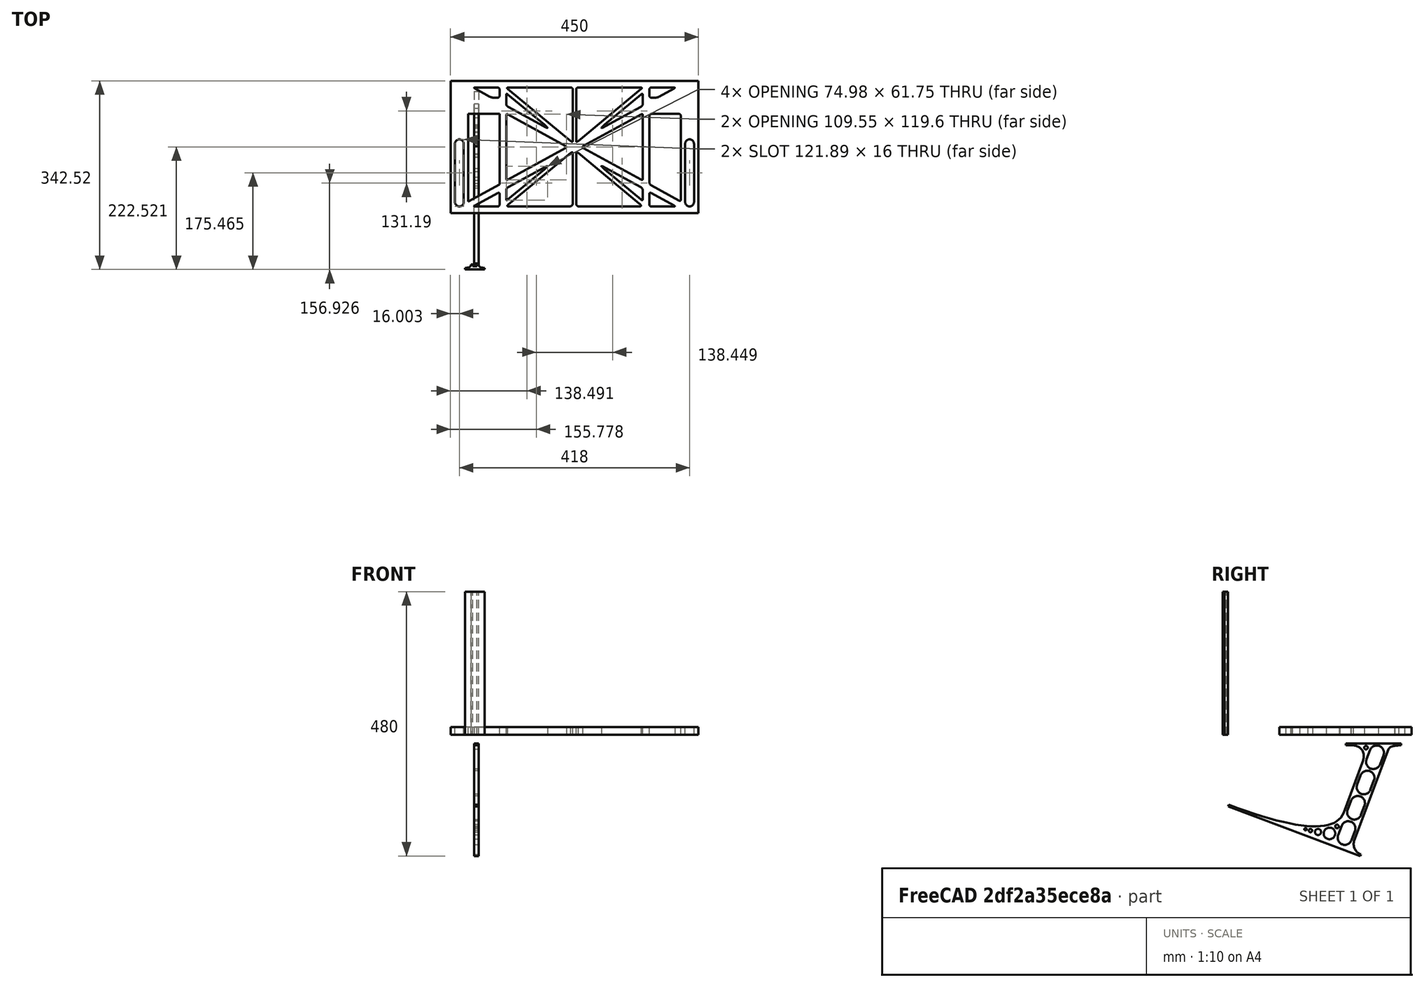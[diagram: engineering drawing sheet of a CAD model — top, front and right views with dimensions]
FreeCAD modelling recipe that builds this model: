
FCSTD DOCUMENT  (FreeCAD 0.19R0.19.2)
Label: laptopStand149FCStd
License: All rights reserved
LicenseURL: http://en.wikipedia.org/wiki/All_rights_reserved
objects: Sketcher::SketchObject×4, Part::Extrusion×3
note: 7 computed .brp shape members not serialized (recipe doc carries the construction recipe); baked Part::Feature solids carry a one-line shape summary decoded from their .brp

FEATURE [Sketcher::SketchObject] Sketch
  FullyConstrained = false
  sketch-geometry (349):
    g0: LineSegment StartX=-10.9272 StartY=-82.7794 StartZ=0 EndX=46.0728 EndY=-51.4823 EndZ=0
    g1: LineSegment StartX=-10.9272 StartY=76.4095 StartZ=0 EndX=-10.9272 EndY=-82.7794 EndZ=0
    g2: LineSegment StartX=46.0728 StartY=76.4095 StartZ=0 EndX=46.0728 EndY=-51.4823 EndZ=0
    g3: LineSegment StartX=-42.9272 StartY=136.221 StartZ=0 EndX=-42.9272 EndY=-103.779 EndZ=0
    g4: LineSegment StartX=407.073 StartY=136.221 StartZ=0 EndX=407.073 EndY=-103.779 EndZ=0
    g5: ArcOfCircle CenterX=-26.9272 CenterY=-83.7794 CenterZ=0 NormalX=0 NormalY=0 NormalZ=1 AngleXU=0 Radius=8 StartAngle=3.14159 EndAngle=6.28319
    g6: ArcOfCircle CenterX=391.073 CenterY=22.1087 CenterZ=0 NormalX=0 NormalY=0 NormalZ=1 AngleXU=0 Radius=8 StartAngle=-4.4e-15 EndAngle=3.14159
    g7: LineSegment StartX=399.073 StartY=22.1087 StartZ=0 EndX=399.073 EndY=-83.7794 EndZ=0
    g8: LineSegment StartX=383.073 StartY=22.1087 StartZ=0 EndX=383.073 EndY=-83.7794 EndZ=0
    g9: ArcOfCircle CenterX=391.073 CenterY=-83.7794 CenterZ=0 NormalX=0 NormalY=0 NormalZ=1 AngleXU=0 Radius=8 StartAngle=3.14159 EndAngle=6.28319
    g10: Circle CenterX=175.022 CenterY=27.0628 CenterZ=0 NormalX=0 NormalY=0 NormalZ=1 AngleXU=0 Radius=1
    g11: Circle CenterX=179.022 CenterY=24.8665 CenterZ=0 NormalX=0 NormalY=0 NormalZ=1 AngleXU=0 Radius=1
    g12: Circle CenterX=179.022 CenterY=27.0628 CenterZ=0 NormalX=0 NormalY=0 NormalZ=1 AngleXU=0 Radius=1
    g13: BSplineCurve PolesCount=3 KnotsCount=2 Degree=2 IsPeriodic=0
    g14: GeomPoint X=175.022 Y=27.0628 Z=0
    g15: GeomPoint X=179.022 Y=27.0628 Z=0
    g16: Circle CenterX=189.124 CenterY=27.0628 CenterZ=0 NormalX=0 NormalY=0 NormalZ=1 AngleXU=0 Radius=1
    g17: Circle CenterX=185.124 CenterY=24.8665 CenterZ=0 NormalX=0 NormalY=0 NormalZ=1 AngleXU=0 Radius=1
    g18: Circle CenterX=185.124 CenterY=27.0628 CenterZ=0 NormalX=0 NormalY=0 NormalZ=1 AngleXU=0 Radius=1
    g19: BSplineCurve PolesCount=3 KnotsCount=2 Degree=2 IsPeriodic=0
    g20: GeomPoint X=189.124 Y=27.0628 Z=0
    g21: GeomPoint X=185.124 Y=27.0628 Z=0
    g22: Circle CenterX=175.022 CenterY=5.37834 CenterZ=0 NormalX=0 NormalY=0 NormalZ=1 AngleXU=0 Radius=1
    g23: Circle CenterX=179.022 CenterY=7.57463 CenterZ=0 NormalX=0 NormalY=0 NormalZ=1 AngleXU=0 Radius=1
    g24: Circle CenterX=179.022 CenterY=5.34704 CenterZ=0 NormalX=0 NormalY=0 NormalZ=1 AngleXU=0 Radius=1
    g25: BSplineCurve PolesCount=3 KnotsCount=2 Degree=2 IsPeriodic=0
    g26: GeomPoint X=175.022 Y=5.37834 Z=0
    g27: GeomPoint X=179.022 Y=5.34704 Z=0
    g28: Circle CenterX=189.124 CenterY=5.37834 CenterZ=0 NormalX=0 NormalY=0 NormalZ=1 AngleXU=0 Radius=1
    g29: Circle CenterX=185.124 CenterY=7.57463 CenterZ=0 NormalX=0 NormalY=0 NormalZ=1 AngleXU=0 Radius=1
    g30: Circle CenterX=185.124 CenterY=5.34704 CenterZ=0 NormalX=0 NormalY=0 NormalZ=1 AngleXU=0 Radius=1
    g31: BSplineCurve PolesCount=3 KnotsCount=2 Degree=2 IsPeriodic=0
    g32: GeomPoint X=189.124 Y=5.37834 Z=0
    g33: GeomPoint X=185.124 Y=5.34704 Z=0
    g34: Circle CenterX=165.871 CenterY=18.1458 CenterZ=0 NormalX=0 NormalY=0 NormalZ=1 AngleXU=0 Radius=1
    g35: Circle CenterX=169.377 CenterY=16.2206 CenterZ=0 NormalX=0 NormalY=0 NormalZ=1 AngleXU=0 Radius=1
    g36: Circle CenterX=165.871 CenterY=14.2954 CenterZ=0 NormalX=0 NormalY=0 NormalZ=1 AngleXU=0 Radius=1
    g37: BSplineCurve PolesCount=3 KnotsCount=2 Degree=2 IsPeriodic=0
    g38: GeomPoint X=165.871 Y=18.1458 Z=0
    g39: GeomPoint X=165.871 Y=14.2954 Z=0
    g40: Circle CenterX=198.275 CenterY=18.1458 CenterZ=0 NormalX=0 NormalY=0 NormalZ=1 AngleXU=0 Radius=1
    g41: Circle CenterX=194.768 CenterY=16.2206 CenterZ=0 NormalX=0 NormalY=0 NormalZ=1 AngleXU=0 Radius=1
    g42: Circle CenterX=198.275 CenterY=14.2954 CenterZ=0 NormalX=0 NormalY=0 NormalZ=1 AngleXU=0 Radius=1
    g43: BSplineCurve PolesCount=3 KnotsCount=2 Degree=2 IsPeriodic=0
    g44: GeomPoint X=198.275 Y=18.1458 Z=0
    g45: GeomPoint X=198.275 Y=14.2954 Z=0
    g46: LineSegment StartX=407.073 StartY=-103.779 StartZ=0 EndX=-42.9272 EndY=-103.779 EndZ=0
    g47: LineSegment StartX=407.073 StartY=136.221 StartZ=0 EndX=-42.9272 EndY=136.221 EndZ=0
    g48: LineSegment StartX=46.0728 StartY=76.4095 StartZ=0 EndX=-10.9272 EndY=76.4095 EndZ=0
    g49: Circle CenterX=125.607 CenterY=54.1951 CenterZ=0 NormalX=0 NormalY=0 NormalZ=1 AngleXU=0 Radius=1
    g50: Circle CenterX=139.632 CenterY=46.4944 CenterZ=0 NormalX=0 NormalY=0 NormalZ=1 AngleXU=0 Radius=1
    g51: Circle CenterX=127.326 CenterY=56.7187 CenterZ=0 NormalX=0 NormalY=0 NormalZ=1 AngleXU=0 Radius=1
    g52: BSplineCurve PolesCount=3 KnotsCount=2 Degree=2 IsPeriodic=0
    g53: GeomPoint X=125.607 Y=54.1951 Z=0
    g54: GeomPoint X=127.326 Y=56.7187 Z=0
    g55: Circle CenterX=236.821 CenterY=56.7187 CenterZ=0 NormalX=0 NormalY=0 NormalZ=1 AngleXU=0 Radius=1
    g56: Circle CenterX=224.513 CenterY=46.4944 CenterZ=0 NormalX=0 NormalY=0 NormalZ=1 AngleXU=0 Radius=1
    g57: Circle CenterX=238.538 CenterY=54.1951 CenterZ=0 NormalX=0 NormalY=0 NormalZ=1 AngleXU=0 Radius=1
    g58: BSplineCurve PolesCount=3 KnotsCount=2 Degree=2 IsPeriodic=0
    g59: GeomPoint X=236.821 Y=56.7187 Z=0
    g60: GeomPoint X=238.538 Y=54.1951 Z=0
    g61: Circle CenterX=238.538 CenterY=-21.7539 CenterZ=0 NormalX=0 NormalY=0 NormalZ=1 AngleXU=0 Radius=1
    g62: Circle CenterX=224.513 CenterY=-14.0532 CenterZ=0 NormalX=0 NormalY=0 NormalZ=1 AngleXU=0 Radius=1
    g63: Circle CenterX=236.821 CenterY=-24.2775 CenterZ=0 NormalX=0 NormalY=0 NormalZ=1 AngleXU=0 Radius=1
    g64: BSplineCurve PolesCount=3 KnotsCount=2 Degree=2 IsPeriodic=0
    g65: GeomPoint X=238.538 Y=-21.7539 Z=0
    g66: GeomPoint X=236.821 Y=-24.2775 Z=0
    g67: Circle CenterX=125.607 CenterY=-21.7539 CenterZ=0 NormalX=0 NormalY=0 NormalZ=1 AngleXU=0 Radius=1
    g68: Circle CenterX=139.632 CenterY=-14.0532 CenterZ=0 NormalX=0 NormalY=0 NormalZ=1 AngleXU=0 Radius=1
    g69: Circle CenterX=127.325 CenterY=-24.2775 CenterZ=0 NormalX=0 NormalY=0 NormalZ=1 AngleXU=0 Radius=1
    g70: BSplineCurve PolesCount=3 KnotsCount=2 Degree=2 IsPeriodic=0
    g71: GeomPoint X=125.607 Y=-21.7539 Z=0
    g72: GeomPoint X=127.325 Y=-24.2775 Z=0
    g73: Circle CenterX=302.996 CenterY=111.695 CenterZ=0 NormalX=0 NormalY=0 NormalZ=1 AngleXU=0 Radius=1
    g74: Circle CenterX=306.073 CenterY=114.251 CenterZ=0 NormalX=0 NormalY=0 NormalZ=1 AngleXU=0 Radius=1
    g75: Circle CenterX=306.073 CenterY=110.251 CenterZ=0 NormalX=0 NormalY=0 NormalZ=1 AngleXU=0 Radius=1
    g76: BSplineCurve PolesCount=3 KnotsCount=2 Degree=2 IsPeriodic=0
    g77: GeomPoint X=302.996 Y=111.695 Z=0
    g78: GeomPoint X=306.073 Y=110.251 Z=0
    g79: Circle CenterX=306.073 CenterY=95.2763 CenterZ=0 NormalX=0 NormalY=0 NormalZ=1 AngleXU=0 Radius=1
    g80: Circle CenterX=306.073 CenterY=91.2763 CenterZ=0 NormalX=0 NormalY=0 NormalZ=1 AngleXU=0 Radius=1
    g81: Circle CenterX=302.567 CenterY=89.3511 CenterZ=0 NormalX=0 NormalY=0 NormalZ=1 AngleXU=0 Radius=1
    g82: BSplineCurve PolesCount=3 KnotsCount=2 Degree=2 IsPeriodic=0
    g83: GeomPoint X=306.073 Y=95.2763 Z=0
    g84: GeomPoint X=302.567 Y=89.3511 Z=0
    g85: LineSegment StartX=306.073 StartY=110.251 StartZ=0 EndX=306.073 EndY=95.2763 EndZ=0
    g86: LineSegment StartX=302.996 StartY=111.695 StartZ=0 EndX=236.821 EndY=56.7187 EndZ=0
    g87: LineSegment StartX=238.538 StartY=54.1951 StartZ=0 EndX=302.567 EndY=89.3511 EndZ=0
    g88: Circle CenterX=61.1496 CenterY=111.695 CenterZ=0 NormalX=0 NormalY=0 NormalZ=1 AngleXU=0 Radius=1
    g89: Circle CenterX=58.0728 CenterY=114.251 CenterZ=0 NormalX=0 NormalY=0 NormalZ=1 AngleXU=0 Radius=1
    g90: Circle CenterX=58.0728 CenterY=110.251 CenterZ=0 NormalX=0 NormalY=0 NormalZ=1 AngleXU=0 Radius=1
    g91: BSplineCurve PolesCount=3 KnotsCount=2 Degree=2 IsPeriodic=0
    g92: GeomPoint X=61.1496 Y=111.695 Z=0
    g93: GeomPoint X=58.0728 Y=110.251 Z=0
    g94: Circle CenterX=61.5791 CenterY=89.3511 CenterZ=0 NormalX=0 NormalY=0 NormalZ=1 AngleXU=0 Radius=1
    g95: Circle CenterX=58.0728 CenterY=91.2763 CenterZ=0 NormalX=0 NormalY=0 NormalZ=1 AngleXU=0 Radius=1
    g96: Circle CenterX=58.0728 CenterY=95.2763 CenterZ=0 NormalX=0 NormalY=0 NormalZ=1 AngleXU=0 Radius=1
    g97: BSplineCurve PolesCount=3 KnotsCount=2 Degree=2 IsPeriodic=0
    g98: GeomPoint X=61.5791 Y=89.3511 Z=0
    g99: GeomPoint X=58.0728 Y=95.2763 Z=0
    g100: LineSegment StartX=58.0728 StartY=110.251 StartZ=0 EndX=58.0728 EndY=95.2763 EndZ=0
    g101: LineSegment StartX=61.1496 StartY=111.695 StartZ=0 EndX=127.326 EndY=56.7187 EndZ=0
    g102: LineSegment StartX=125.607 StartY=54.1951 StartZ=0 EndX=61.5791 EndY=89.3511 EndZ=0
    g103: Circle CenterX=61.5791 CenterY=-56.9099 CenterZ=0 NormalX=0 NormalY=0 NormalZ=1 AngleXU=0 Radius=1
    g104: Circle CenterX=58.0728 CenterY=-58.8351 CenterZ=0 NormalX=0 NormalY=0 NormalZ=1 AngleXU=0 Radius=1
    g105: Circle CenterX=58.0728 CenterY=-62.8351 CenterZ=0 NormalX=0 NormalY=0 NormalZ=1 AngleXU=0 Radius=1
    g106: BSplineCurve PolesCount=3 KnotsCount=2 Degree=2 IsPeriodic=0
    g107: GeomPoint X=61.5791 Y=-56.9099 Z=0
    g108: GeomPoint X=58.0728 Y=-62.8351 Z=0
    g109: Circle CenterX=58.0728 CenterY=-77.8102 CenterZ=0 NormalX=0 NormalY=0 NormalZ=1 AngleXU=0 Radius=1
    g110: Circle CenterX=58.0728 CenterY=-81.8102 CenterZ=0 NormalX=0 NormalY=0 NormalZ=1 AngleXU=0 Radius=1
    g111: Circle CenterX=61.1496 CenterY=-79.2541 CenterZ=0 NormalX=0 NormalY=0 NormalZ=1 AngleXU=0 Radius=1
    g112: BSplineCurve PolesCount=3 KnotsCount=2 Degree=2 IsPeriodic=0
    g113: GeomPoint X=58.0728 Y=-77.8102 Z=0
    g114: GeomPoint X=61.1496 Y=-79.2541 Z=0
    g115: LineSegment StartX=58.0728 StartY=-62.8351 StartZ=0 EndX=58.0728 EndY=-77.8102 EndZ=0
    g116: LineSegment StartX=61.1496 StartY=-79.2541 StartZ=0 EndX=127.325 EndY=-24.2775 EndZ=0
    g117: LineSegment StartX=125.607 StartY=-21.7539 StartZ=0 EndX=61.5791 EndY=-56.9099 EndZ=0
    g118: Circle CenterX=302.567 CenterY=-56.9099 CenterZ=0 NormalX=0 NormalY=0 NormalZ=1 AngleXU=0 Radius=1
    g119: Circle CenterX=306.073 CenterY=-58.8351 CenterZ=0 NormalX=0 NormalY=0 NormalZ=1 AngleXU=0 Radius=1
    g120: Circle CenterX=306.073 CenterY=-62.8351 CenterZ=0 NormalX=0 NormalY=0 NormalZ=1 AngleXU=0 Radius=1
    g121: BSplineCurve PolesCount=3 KnotsCount=2 Degree=2 IsPeriodic=0
    g122: GeomPoint X=302.567 Y=-56.9099 Z=0
    g123: GeomPoint X=306.073 Y=-62.8351 Z=0
    g124: Circle CenterX=302.996 CenterY=-79.2541 CenterZ=0 NormalX=0 NormalY=0 NormalZ=1 AngleXU=0 Radius=1
    g125: Circle CenterX=306.073 CenterY=-81.8102 CenterZ=0 NormalX=0 NormalY=0 NormalZ=1 AngleXU=0 Radius=1
    g126: Circle CenterX=306.073 CenterY=-77.8102 CenterZ=0 NormalX=0 NormalY=0 NormalZ=1 AngleXU=0 Radius=1
    g127: BSplineCurve PolesCount=3 KnotsCount=2 Degree=2 IsPeriodic=0
    g128: GeomPoint X=302.996 Y=-79.2541 Z=0
    g129: GeomPoint X=306.073 Y=-77.8102 Z=0
    g130: LineSegment StartX=306.073 StartY=-62.8351 StartZ=0 EndX=306.073 EndY=-77.8102 EndZ=0
    g131: LineSegment StartX=302.996 StartY=-79.2541 StartZ=0 EndX=236.821 EndY=-24.2775 EndZ=0
    g132: LineSegment StartX=238.538 StartY=-21.7539 StartZ=0 EndX=302.567 EndY=-56.9099 EndZ=0
    g133: Circle CenterX=61.6457 CenterY=-88.8112 CenterZ=0 NormalX=0 NormalY=0 NormalZ=1 AngleXU=0 Radius=1
    g134: Circle CenterX=58.0728 CenterY=-91.7794 CenterZ=0 NormalX=0 NormalY=0 NormalZ=1 AngleXU=0 Radius=1
    g135: Circle CenterX=63.9135 CenterY=-91.7794 CenterZ=0 NormalX=0 NormalY=0 NormalZ=1 AngleXU=0 Radius=1
    g136: BSplineCurve PolesCount=3 KnotsCount=2 Degree=2 IsPeriodic=0
    g137: GeomPoint X=61.6457 Y=-88.8112 Z=0
    g138: GeomPoint X=63.9135 Y=-91.7794 Z=0
    g139: Circle CenterX=179.022 CenterY=-85.8163 CenterZ=0 NormalX=0 NormalY=0 NormalZ=1 AngleXU=0 Radius=1
    g140: Circle CenterX=179.022 CenterY=-91.7794 CenterZ=0 NormalX=0 NormalY=0 NormalZ=1 AngleXU=0 Radius=1
    g141: Circle CenterX=171.895 CenterY=-91.7794 CenterZ=0 NormalX=0 NormalY=0 NormalZ=1 AngleXU=0 Radius=1
    g142: BSplineCurve PolesCount=3 KnotsCount=2 Degree=2 IsPeriodic=0
    g143: GeomPoint X=179.022 Y=-85.8163 Z=0
    g144: GeomPoint X=171.895 Y=-91.7794 Z=0
    g145: Circle CenterX=185.124 CenterY=-86.2028 CenterZ=0 NormalX=0 NormalY=0 NormalZ=1 AngleXU=0 Radius=1
    g146: Circle CenterX=185.124 CenterY=-91.7794 CenterZ=0 NormalX=0 NormalY=0 NormalZ=1 AngleXU=0 Radius=1
    g147: Circle CenterX=191.747 CenterY=-91.7794 CenterZ=0 NormalX=0 NormalY=0 NormalZ=1 AngleXU=0 Radius=1
    g148: BSplineCurve PolesCount=3 KnotsCount=2 Degree=2 IsPeriodic=0
    g149: GeomPoint X=185.124 Y=-86.2028 Z=0
    g150: GeomPoint X=191.747 Y=-91.7794 Z=0
    g151: Circle CenterX=299.888 CenterY=-86.6413 CenterZ=0 NormalX=0 NormalY=0 NormalZ=1 AngleXU=0 Radius=1
    g152: Circle CenterX=306.073 CenterY=-91.7794 CenterZ=0 NormalX=0 NormalY=0 NormalZ=1 AngleXU=0 Radius=1
    g153: Circle CenterX=298.776 CenterY=-91.7794 CenterZ=0 NormalX=0 NormalY=0 NormalZ=1 AngleXU=0 Radius=1
    g154: BSplineCurve PolesCount=3 KnotsCount=2 Degree=2 IsPeriodic=0
    g155: GeomPoint X=299.888 Y=-86.6413 Z=0
    g156: GeomPoint X=298.776 Y=-91.7794 Z=0
    g157: LineSegment StartX=189.124 StartY=5.37834 StartZ=0 EndX=299.888 EndY=-86.6413 EndZ=0
    g158: LineSegment StartX=298.776 StartY=-91.7794 StartZ=0 EndX=191.747 EndY=-91.7794 EndZ=0
    g159: LineSegment StartX=185.124 StartY=-86.2028 StartZ=0 EndX=185.124 EndY=5.34704 EndZ=0
    g160: LineSegment StartX=179.022 StartY=5.34704 StartZ=0 EndX=179.022 EndY=-85.8163 EndZ=0
    g161: LineSegment StartX=171.895 StartY=-91.7794 StartZ=0 EndX=63.9135 EndY=-91.7794 EndZ=0
    g162: LineSegment StartX=61.6457 StartY=-88.8112 StartZ=0 EndX=175.022 EndY=5.37834 EndZ=0
    g163: Circle CenterX=302.073 CenterY=124.221 CenterZ=0 NormalX=0 NormalY=0 NormalZ=1 AngleXU=0 Radius=1
    g164: Circle CenterX=306.073 CenterY=124.221 CenterZ=0 NormalX=0 NormalY=0 NormalZ=1 AngleXU=0 Radius=1
    g165: Circle CenterX=302.996 CenterY=121.665 CenterZ=0 NormalX=0 NormalY=0 NormalZ=1 AngleXU=0 Radius=1
    g166: BSplineCurve PolesCount=3 KnotsCount=2 Degree=2 IsPeriodic=0
    g167: GeomPoint X=302.073 Y=124.221 Z=0
    g168: GeomPoint X=302.996 Y=121.665 Z=0
    g169: Circle CenterX=189.124 CenterY=124.221 CenterZ=0 NormalX=0 NormalY=0 NormalZ=1 AngleXU=0 Radius=1
    g170: Circle CenterX=185.124 CenterY=124.221 CenterZ=0 NormalX=0 NormalY=0 NormalZ=1 AngleXU=0 Radius=1
    g171: Circle CenterX=185.124 CenterY=120.221 CenterZ=0 NormalX=0 NormalY=0 NormalZ=1 AngleXU=0 Radius=1
    g172: BSplineCurve PolesCount=3 KnotsCount=2 Degree=2 IsPeriodic=0
    g173: GeomPoint X=189.124 Y=124.221 Z=0
    g174: GeomPoint X=185.124 Y=120.221 Z=0
    g175: Circle CenterX=175.022 CenterY=124.221 CenterZ=0 NormalX=0 NormalY=0 NormalZ=1 AngleXU=0 Radius=1
    g176: Circle CenterX=179.022 CenterY=124.221 CenterZ=0 NormalX=0 NormalY=0 NormalZ=1 AngleXU=0 Radius=1
    g177: Circle CenterX=179.022 CenterY=120.221 CenterZ=0 NormalX=0 NormalY=0 NormalZ=1 AngleXU=0 Radius=1
    g178: BSplineCurve PolesCount=3 KnotsCount=2 Degree=2 IsPeriodic=0
    g179: GeomPoint X=175.022 Y=124.221 Z=0
    g180: GeomPoint X=179.022 Y=120.221 Z=0
    g181: Circle CenterX=62.0728 CenterY=124.221 CenterZ=0 NormalX=0 NormalY=0 NormalZ=1 AngleXU=0 Radius=1
    g182: Circle CenterX=58.0728 CenterY=124.221 CenterZ=0 NormalX=0 NormalY=0 NormalZ=1 AngleXU=0 Radius=1
    g183: Circle CenterX=61.1496 CenterY=121.665 CenterZ=0 NormalX=0 NormalY=0 NormalZ=1 AngleXU=0 Radius=1
    g184: BSplineCurve PolesCount=3 KnotsCount=2 Degree=2 IsPeriodic=0
    g185: GeomPoint X=62.0728 Y=124.221 Z=0
    g186: GeomPoint X=61.1496 Y=121.665 Z=0
    g187: LineSegment StartX=62.0728 StartY=124.221 StartZ=0 EndX=175.022 EndY=124.221 EndZ=0
    g188: LineSegment StartX=179.022 StartY=120.221 StartZ=0 EndX=179.022 EndY=27.0628 EndZ=0
    g189: LineSegment StartX=185.124 StartY=27.0628 StartZ=0 EndX=185.124 EndY=120.221 EndZ=0
    g190: LineSegment StartX=189.124 StartY=124.221 StartZ=0 EndX=302.073 EndY=124.221 EndZ=0
    g191: LineSegment StartX=302.996 StartY=121.665 StartZ=0 EndX=189.124 EndY=27.0628 EndZ=0
    g192: LineSegment StartX=175.022 StartY=27.0628 StartZ=0 EndX=61.1496 EndY=121.665 EndZ=0
    g193: Circle CenterX=61.5791 CenterY=75.4095 CenterZ=0 NormalX=0 NormalY=0 NormalZ=1 AngleXU=0 Radius=1
    g194: Circle CenterX=58.0728 CenterY=77.3346 CenterZ=0 NormalX=0 NormalY=0 NormalZ=1 AngleXU=0 Radius=1
    g195: Circle CenterX=58.0728 CenterY=73.3346 CenterZ=0 NormalX=0 NormalY=0 NormalZ=1 AngleXU=0 Radius=1
    g196: BSplineCurve PolesCount=3 KnotsCount=2 Degree=2 IsPeriodic=0
    g197: GeomPoint X=61.5791 Y=75.4095 Z=0
    g198: GeomPoint X=58.0728 Y=73.3346 Z=0
    g199: Circle CenterX=58.0728 CenterY=-40.8935 CenterZ=0 NormalX=0 NormalY=0 NormalZ=1 AngleXU=0 Radius=1
    g200: Circle CenterX=58.0728 CenterY=-44.8935 CenterZ=0 NormalX=0 NormalY=0 NormalZ=1 AngleXU=0 Radius=1
    g201: Circle CenterX=61.5791 CenterY=-42.9683 CenterZ=0 NormalX=0 NormalY=0 NormalZ=1 AngleXU=0 Radius=1
    g202: BSplineCurve PolesCount=3 KnotsCount=2 Degree=2 IsPeriodic=0
    g203: GeomPoint X=58.0728 Y=-40.8935 Z=0
    g204: GeomPoint X=61.5791 Y=-42.9683 Z=0
    g205: LineSegment StartX=61.5791 StartY=-42.9683 StartZ=0 EndX=165.871 EndY=14.2954 EndZ=0
    g206: LineSegment StartX=165.871 StartY=18.1458 StartZ=0 EndX=61.5791 EndY=75.4095 EndZ=0
    g207: LineSegment StartX=58.0728 StartY=73.3346 StartZ=0 EndX=58.0728 EndY=-40.8935 EndZ=0
    g208: Circle CenterX=302.567 CenterY=-42.9683 CenterZ=0 NormalX=0 NormalY=0 NormalZ=1 AngleXU=0 Radius=1
    g209: Circle CenterX=306.073 CenterY=-44.8935 CenterZ=0 NormalX=0 NormalY=0 NormalZ=1 AngleXU=0 Radius=1
    g210: Circle CenterX=306.073 CenterY=-40.8935 CenterZ=0 NormalX=0 NormalY=0 NormalZ=1 AngleXU=0 Radius=1
    g211: BSplineCurve PolesCount=3 KnotsCount=2 Degree=2 IsPeriodic=0
    g212: GeomPoint X=302.567 Y=-42.9683 Z=0
    g213: GeomPoint X=306.073 Y=-40.8935 Z=0
    g214: Circle CenterX=306.073 CenterY=73.3346 CenterZ=0 NormalX=0 NormalY=0 NormalZ=1 AngleXU=0 Radius=1
    g215: Circle CenterX=306.073 CenterY=77.3346 CenterZ=0 NormalX=0 NormalY=0 NormalZ=1 AngleXU=0 Radius=1
    g216: Circle CenterX=302.567 CenterY=75.4095 CenterZ=0 NormalX=0 NormalY=0 NormalZ=1 AngleXU=0 Radius=1
    g217: BSplineCurve PolesCount=3 KnotsCount=2 Degree=2 IsPeriodic=0
    g218: GeomPoint X=306.073 Y=73.3346 Z=0
    g219: GeomPoint X=302.567 Y=75.4095 Z=0
    g220: LineSegment StartX=302.567 StartY=-42.9683 StartZ=0 EndX=198.275 EndY=14.2954 EndZ=0
    g221: LineSegment StartX=198.275 StartY=18.1458 StartZ=0 EndX=302.567 EndY=75.4095 EndZ=0
    g222: LineSegment StartX=306.073 StartY=73.3346 StartZ=0 EndX=306.073 EndY=-40.8935 EndZ=0
    g223: LineSegment StartX=322.073 StartY=105.865 StartZ=0 EndX=328.643 EndY=105.865 EndZ=0
    g224: LineSegment StartX=318.073 StartY=120.221 StartZ=0 EndX=318.073 EndY=109.865 EndZ=0
    g225: LineSegment StartX=336.157 StartY=107.779 StartZ=0 EndX=362.567 EndY=122.294 EndZ=0
    g226: Circle CenterX=362.073 CenterY=124.221 CenterZ=0 NormalX=0 NormalY=0 NormalZ=1 AngleXU=0 Radius=1
    g227: Circle CenterX=366.073 CenterY=124.221 CenterZ=0 NormalX=0 NormalY=0 NormalZ=1 AngleXU=0 Radius=1
    g228: Circle CenterX=362.567 CenterY=122.294 CenterZ=0 NormalX=0 NormalY=0 NormalZ=1 AngleXU=0 Radius=1
    g229: BSplineCurve PolesCount=3 KnotsCount=2 Degree=2 IsPeriodic=0
    g230: GeomPoint X=362.073 Y=124.221 Z=0
    g231: GeomPoint X=362.567 Y=122.294 Z=0
    g232: Circle CenterX=322.073 CenterY=124.221 CenterZ=0 NormalX=0 NormalY=0 NormalZ=1 AngleXU=0 Radius=1
    g233: Circle CenterX=318.073 CenterY=124.221 CenterZ=0 NormalX=0 NormalY=0 NormalZ=1 AngleXU=0 Radius=1
    g234: Circle CenterX=318.073 CenterY=120.221 CenterZ=0 NormalX=0 NormalY=0 NormalZ=1 AngleXU=0 Radius=1
    g235: BSplineCurve PolesCount=3 KnotsCount=2 Degree=2 IsPeriodic=0
    g236: GeomPoint X=322.073 Y=124.221 Z=0
    g237: GeomPoint X=318.073 Y=120.221 Z=0
    g238: Circle CenterX=322.073 CenterY=105.865 CenterZ=0 NormalX=0 NormalY=0 NormalZ=1 AngleXU=0 Radius=1
    g239: Circle CenterX=318.073 CenterY=105.865 CenterZ=0 NormalX=0 NormalY=0 NormalZ=1 AngleXU=0 Radius=1
    g240: Circle CenterX=318.073 CenterY=109.865 CenterZ=0 NormalX=0 NormalY=0 NormalZ=1 AngleXU=0 Radius=1
    g241: BSplineCurve PolesCount=3 KnotsCount=2 Degree=2 IsPeriodic=0
    g242: GeomPoint X=322.073 Y=105.865 Z=0
    g243: GeomPoint X=318.073 Y=109.865 Z=0
    g244: Circle CenterX=336.157 CenterY=107.779 CenterZ=0 NormalX=0 NormalY=0 NormalZ=1 AngleXU=0 Radius=1
    g245: Circle CenterX=332.651 CenterY=105.853 CenterZ=0 NormalX=0 NormalY=0 NormalZ=1 AngleXU=0 Radius=1
    g246: Circle CenterX=328.643 CenterY=105.865 CenterZ=0 NormalX=0 NormalY=0 NormalZ=1 AngleXU=0 Radius=1
    g247: BSplineCurve PolesCount=3 KnotsCount=2 Degree=2 IsPeriodic=0
    g248: GeomPoint X=336.157 Y=107.779 Z=0
    g249: GeomPoint X=328.643 Y=105.865 Z=0
    g250: LineSegment StartX=322.073 StartY=124.221 StartZ=0 EndX=362.073 EndY=124.221 EndZ=0
    g251: Circle CenterX=371.567 CenterY=-80.8644 CenterZ=0 NormalX=0 NormalY=0 NormalZ=1 AngleXU=0 Radius=1
    g252: Circle CenterX=375.073 CenterY=-82.7896 CenterZ=0 NormalX=0 NormalY=0 NormalZ=1 AngleXU=0 Radius=1
    g253: Circle CenterX=375.073 CenterY=-78.7896 CenterZ=0 NormalX=0 NormalY=0 NormalZ=1 AngleXU=0 Radius=1
    g254: BSplineCurve PolesCount=3 KnotsCount=2 Degree=2 IsPeriodic=0
    g255: GeomPoint X=371.567 Y=-80.8644 Z=0
    g256: GeomPoint X=375.073 Y=-78.7896 Z=0
    g257: Circle CenterX=321.579 CenterY=-53.4075 CenterZ=0 NormalX=0 NormalY=0 NormalZ=1 AngleXU=0 Radius=1
    g258: Circle CenterX=318.073 CenterY=-51.4823 CenterZ=0 NormalX=0 NormalY=0 NormalZ=1 AngleXU=0 Radius=1
    g259: Circle CenterX=318.073 CenterY=-47.4805 CenterZ=0 NormalX=0 NormalY=0 NormalZ=1 AngleXU=0 Radius=1
    g260: BSplineCurve PolesCount=3 KnotsCount=2 Degree=2 IsPeriodic=0
    g261: GeomPoint X=321.579 Y=-53.4075 Z=0
    g262: GeomPoint X=318.073 Y=-47.4805 Z=0
    g263: LineSegment StartX=371.567 StartY=-80.8644 StartZ=0 EndX=321.579 EndY=-53.4075 EndZ=0
    g264: Circle CenterX=321.579 CenterY=-67.3492 CenterZ=0 NormalX=0 NormalY=0 NormalZ=1 AngleXU=0 Radius=1
    g265: Circle CenterX=318.073 CenterY=-65.424 CenterZ=0 NormalX=0 NormalY=0 NormalZ=1 AngleXU=0 Radius=1
    g266: Circle CenterX=318.073 CenterY=-69.424 CenterZ=0 NormalX=0 NormalY=0 NormalZ=1 AngleXU=0 Radius=1
    g267: BSplineCurve PolesCount=3 KnotsCount=2 Degree=2 IsPeriodic=0
    g268: GeomPoint X=321.579 Y=-67.3492 Z=0
    g269: GeomPoint X=318.073 Y=-69.424 Z=0
    g270: Circle CenterX=362.567 CenterY=-89.8542 CenterZ=0 NormalX=0 NormalY=0 NormalZ=1 AngleXU=0 Radius=1
    g271: Circle CenterX=366.073 CenterY=-91.7794 CenterZ=0 NormalX=0 NormalY=0 NormalZ=1 AngleXU=0 Radius=1
    g272: Circle CenterX=362.073 CenterY=-91.7794 CenterZ=0 NormalX=0 NormalY=0 NormalZ=1 AngleXU=0 Radius=1
    g273: BSplineCurve PolesCount=3 KnotsCount=2 Degree=2 IsPeriodic=0
    g274: GeomPoint X=362.567 Y=-89.8542 Z=0
    g275: GeomPoint X=362.073 Y=-91.7794 Z=0
    g276: Circle CenterX=322.073 CenterY=-91.7794 CenterZ=0 NormalX=0 NormalY=0 NormalZ=1 AngleXU=0 Radius=1
    g277: Circle CenterX=318.073 CenterY=-91.7794 CenterZ=0 NormalX=0 NormalY=0 NormalZ=1 AngleXU=0 Radius=1
    g278: Circle CenterX=318.073 CenterY=-87.7794 CenterZ=0 NormalX=0 NormalY=0 NormalZ=1 AngleXU=0 Radius=1
    g279: BSplineCurve PolesCount=3 KnotsCount=2 Degree=2 IsPeriodic=0
    g280: GeomPoint X=322.073 Y=-91.7794 Z=0
    g281: GeomPoint X=318.073 Y=-87.7794 Z=0
    g282: LineSegment StartX=362.567 StartY=-89.8542 StartZ=0 EndX=321.579 EndY=-67.3492 EndZ=0
    g283: LineSegment StartX=318.073 StartY=-69.424 StartZ=0 EndX=318.073 EndY=-87.7794 EndZ=0
    g284: LineSegment StartX=322.073 StartY=-91.7794 StartZ=0 EndX=362.073 EndY=-91.7794 EndZ=0
    g285: Circle CenterX=2.07281 CenterY=124.221 CenterZ=0 NormalX=0 NormalY=0 NormalZ=1 AngleXU=0 Radius=1
    g286: Circle CenterX=1.57905 CenterY=122.295 CenterZ=0 NormalX=0 NormalY=0 NormalZ=1 AngleXU=0 Radius=1
    g287: BSplineCurve PolesCount=3 KnotsCount=2 Degree=2 IsPeriodic=0
    g288: GeomPoint X=2.07281 Y=124.221 Z=0
    g289: GeomPoint X=1.57905 Y=122.295 Z=0
    g290: Circle CenterX=42.0728 CenterY=124.221 CenterZ=0 NormalX=0 NormalY=0 NormalZ=1 AngleXU=0 Radius=1
    g291: Circle CenterX=46.0728 CenterY=124.221 CenterZ=0 NormalX=0 NormalY=0 NormalZ=1 AngleXU=0 Radius=1
    g292: Circle CenterX=46.0728 CenterY=120.221 CenterZ=0 NormalX=0 NormalY=0 NormalZ=1 AngleXU=0 Radius=1
    g293: BSplineCurve PolesCount=3 KnotsCount=2 Degree=2 IsPeriodic=0
    g294: GeomPoint X=42.0728 Y=124.221 Z=0
    g295: GeomPoint X=46.0728 Y=120.221 Z=0
    g296: Circle CenterX=46.0728 CenterY=109.865 CenterZ=0 NormalX=0 NormalY=0 NormalZ=1 AngleXU=0 Radius=1
    g297: Circle CenterX=46.0728 CenterY=105.865 CenterZ=0 NormalX=0 NormalY=0 NormalZ=1 AngleXU=0 Radius=1
    g298: Circle CenterX=42.0728 CenterY=105.865 CenterZ=0 NormalX=0 NormalY=0 NormalZ=1 AngleXU=0 Radius=1
    g299: BSplineCurve PolesCount=3 KnotsCount=2 Degree=2 IsPeriodic=0
    g300: GeomPoint X=46.0728 Y=109.865 Z=0
    g301: GeomPoint X=42.0728 Y=105.865 Z=0
    g302: Circle CenterX=35.5028 CenterY=105.865 CenterZ=0 NormalX=0 NormalY=0 NormalZ=1 AngleXU=0 Radius=1
    g303: Circle CenterX=31.5028 CenterY=105.865 CenterZ=0 NormalX=0 NormalY=0 NormalZ=1 AngleXU=0 Radius=1
    g304: Circle CenterX=27.9965 CenterY=107.79 CenterZ=0 NormalX=0 NormalY=0 NormalZ=1 AngleXU=0 Radius=1
    g305: BSplineCurve PolesCount=3 KnotsCount=2 Degree=2 IsPeriodic=0
    g306: GeomPoint X=35.5028 Y=105.865 Z=0
    g307: GeomPoint X=27.9965 Y=107.79 Z=0
    g308: LineSegment StartX=2.07281 StartY=124.221 StartZ=0 EndX=42.0728 EndY=124.221 EndZ=0
    g309: LineSegment StartX=46.0728 StartY=120.221 StartZ=0 EndX=46.0728 EndY=109.865 EndZ=0
    g310: LineSegment StartX=42.0728 StartY=105.865 StartZ=0 EndX=35.5028 EndY=105.865 EndZ=0
    g311: LineSegment StartX=27.9965 StartY=107.79 StartZ=0 EndX=1.57905 EndY=122.295 EndZ=0
    g312: Circle CenterX=42.5666 CenterY=-67.3492 CenterZ=0 NormalX=0 NormalY=0 NormalZ=1 AngleXU=0 Radius=1
    g313: Circle CenterX=46.0728 CenterY=-65.424 CenterZ=0 NormalX=0 NormalY=0 NormalZ=1 AngleXU=0 Radius=1
    g314: Circle CenterX=46.0728 CenterY=-69.424 CenterZ=0 NormalX=0 NormalY=0 NormalZ=1 AngleXU=0 Radius=1
    g315: BSplineCurve PolesCount=3 KnotsCount=2 Degree=2 IsPeriodic=0
    g316: GeomPoint X=42.5666 Y=-67.3492 Z=0
    g317: GeomPoint X=46.0728 Y=-69.424 Z=0
    g318: Circle CenterX=46.0728 CenterY=-87.7794 CenterZ=0 NormalX=0 NormalY=0 NormalZ=1 AngleXU=0 Radius=1
    g319: Circle CenterX=46.0728 CenterY=-91.7794 CenterZ=0 NormalX=0 NormalY=0 NormalZ=1 AngleXU=0 Radius=1
    g320: Circle CenterX=42.0728 CenterY=-91.7794 CenterZ=0 NormalX=0 NormalY=0 NormalZ=1 AngleXU=0 Radius=1
    g321: BSplineCurve PolesCount=3 KnotsCount=2 Degree=2 IsPeriodic=0
    g322: GeomPoint X=46.0728 Y=-87.7794 Z=0
    g323: GeomPoint X=42.0728 Y=-91.7794 Z=0
    g324: Circle CenterX=2.07281 CenterY=-91.7794 CenterZ=0 NormalX=0 NormalY=0 NormalZ=1 AngleXU=0 Radius=1
    g325: Circle CenterX=-1.92719 CenterY=-91.7794 CenterZ=0 NormalX=0 NormalY=0 NormalZ=1 AngleXU=0 Radius=1
    g326: Circle CenterX=1.57905 CenterY=-89.8542 CenterZ=0 NormalX=0 NormalY=0 NormalZ=1 AngleXU=0 Radius=1
    g327: BSplineCurve PolesCount=3 KnotsCount=2 Degree=2 IsPeriodic=0
    g328: GeomPoint X=2.07281 Y=-91.7794 Z=0
    g329: GeomPoint X=1.57905 Y=-89.8542 Z=0
    g330: LineSegment StartX=2.07281 StartY=-91.7794 StartZ=0 EndX=42.0728 EndY=-91.7794 EndZ=0
    g331: LineSegment StartX=46.0728 StartY=-87.7794 StartZ=0 EndX=46.0728 EndY=-69.424 EndZ=0
    g332: LineSegment StartX=42.5666 StartY=-67.3492 StartZ=0 EndX=1.57905 EndY=-89.8542 EndZ=0
    g333: Circle CenterX=322.073 CenterY=76.4095 CenterZ=0 NormalX=0 NormalY=0 NormalZ=1 AngleXU=0 Radius=4
    g334: BSplineCurve PolesCount=3 KnotsCount=2 Degree=2 IsPeriodic=0
    g335: GeomPoint X=318.073 Y=72.4095 Z=0
    g336: GeomPoint X=322.073 Y=76.4095 Z=0
    g337: Circle CenterX=375.073 CenterY=72.4095 CenterZ=0 NormalX=0 NormalY=0 NormalZ=1 AngleXU=0 Radius=1
    g338: Circle CenterX=375.073 CenterY=76.4095 CenterZ=0 NormalX=0 NormalY=0 NormalZ=1 AngleXU=0 Radius=1
    g339: Circle CenterX=371.073 CenterY=76.4095 CenterZ=0 NormalX=0 NormalY=0 NormalZ=1 AngleXU=0 Radius=1
    g340: BSplineCurve PolesCount=3 KnotsCount=2 Degree=2 IsPeriodic=0
    g341: GeomPoint X=375.073 Y=72.4095 Z=0
    g342: GeomPoint X=371.073 Y=76.4095 Z=0
    g343: LineSegment StartX=322.073 StartY=76.4095 StartZ=0 EndX=371.073 EndY=76.4095 EndZ=0
    g344: LineSegment StartX=318.073 StartY=72.4095 StartZ=0 EndX=318.073 EndY=-47.4805 EndZ=0
    g345: LineSegment StartX=375.073 StartY=72.4095 StartZ=0 EndX=375.073 EndY=-78.7896 EndZ=0
    g346: ArcOfCircle CenterX=-26.9272 CenterY=22.1087 CenterZ=0 NormalX=0 NormalY=0 NormalZ=1 AngleXU=0 Radius=4 StartAngle=5e-16 EndAngle=3.14159
    g347: LineSegment StartX=-30.9272 StartY=22.1087 StartZ=0 EndX=-34.9272 EndY=-83.7794 EndZ=0
    g348: LineSegment StartX=-18.9272 StartY=-83.7794 StartZ=0 EndX=-22.9272 EndY=22.1087 EndZ=0
  constraints (572):
    c: Coincident(g0,g2)
    c: Block(g0)
    c: Block(g1)
    c: Vertical(g3)
    c: Vertical(g4)
    c: Block(g4)
    c: Block(g3)
    c: Tangent(g6,g7) = 1.5708
    c: Tangent(g7,g9) = 1.5708
    c: Equal(g6,g9)
    c: Coincident(g8,g6)
    c: Coincident(g8,g9)
    c: Block(g7)
    c: Block(g8)
    c: Weight(g10) = 1
    c: Equal(g10,g11)
    c: Equal(g10,g12)
    c: InternalAlignment(g10,g13)
    c: InternalAlignment(g11,g13)
    c: InternalAlignment(g12,g13)
    c: InternalAlignment(g14,g13)
    c: InternalAlignment(g15,g13)
    c: Weight(g16) = 1
    c: Equal(g16,g17)
    c: Equal(g16,g18)
    c: InternalAlignment(g16,g19)
    c: InternalAlignment(g17,g19)
    c: InternalAlignment(g18,g19)
    c: InternalAlignment(g20,g19)
    c: InternalAlignment(g21,g19)
    c: Block(g19)
    c: Block(g13)
    c: Weight(g22) = 1
    c: Equal(g22,g23)
    c: Equal(g22,g24)
    c: InternalAlignment(g22,g25)
    c: InternalAlignment(g23,g25)
    c: InternalAlignment(g24,g25)
    c: InternalAlignment(g26,g25)
    c: InternalAlignment(g27,g25)
    c: Weight(g28) = 1
    c: Equal(g28,g29)
    c: Equal(g28,g30)
    c: InternalAlignment(g28,g31)
    c: InternalAlignment(g29,g31)
    c: InternalAlignment(g30,g31)
    c: InternalAlignment(g32,g31)
    c: InternalAlignment(g33,g31)
    c: Block(g31)
    c: Block(g25)
    c: Weight(g34) = 1
    c: Equal(g34,g35)
    c: Equal(g34,g36)
    c: InternalAlignment(g34,g37)
    c: InternalAlignment(g35,g37)
    c: InternalAlignment(g36,g37)
    c: InternalAlignment(g38,g37)
    c: InternalAlignment(g39,g37)
    c: Weight(g40) = 1
    c: Equal(g40,g41)
    c: Equal(g40,g42)
    c: InternalAlignment(g40,g43)
    c: InternalAlignment(g41,g43)
    c: InternalAlignment(g42,g43)
    c: InternalAlignment(g44,g43)
    c: InternalAlignment(g45,g43)
    c: Block(g37)
    c: Block(g43)
    c: Coincident(g46,g4)
    c: Coincident(g46,g3)
    c: Horizontal(g46)
    c: Distance(g46) = 450
    c: Coincident(g47,g4)
    c: Coincident(g47,g3)
    c: Horizontal(g47)
    c: Horizontal(g48)
    c: Coincident(g2,g48)
    c: Block(g48)
    c: Coincident(g1,g48)
    c: Weight(g49) = 1
    c: Equal(g49,g50)
    c: Equal(g49,g51)
    c: InternalAlignment(g49,g52)
    c: InternalAlignment(g50,g52)
    c: InternalAlignment(g51,g52)
    c: InternalAlignment(g53,g52)
    c: InternalAlignment(g54,g52)
    c: Block(g52)
    c: Weight(g55) = 1
    c: Equal(g55,g56)
    c: Equal(g55,g57)
    c: InternalAlignment(g55,g58)
    c: InternalAlignment(g56,g58)
    c: InternalAlignment(g57,g58)
    c: InternalAlignment(g59,g58)
    c: InternalAlignment(g60,g58)
    c: Block(g58)
    c: Weight(g61) = 1
    c: Equal(g61,g62)
    c: Equal(g61,g63)
    c: InternalAlignment(g61,g64)
    c: InternalAlignment(g62,g64)
    c: InternalAlignment(g63,g64)
    c: InternalAlignment(g65,g64)
    c: InternalAlignment(g66,g64)
    c: Block(g64)
    c: Weight(g67) = 1
    c: Equal(g67,g68)
    c: Equal(g67,g69)
    c: InternalAlignment(g67,g70)
    c: InternalAlignment(g68,g70)
    c: InternalAlignment(g69,g70)
    c: InternalAlignment(g71,g70)
    c: InternalAlignment(g72,g70)
    c: Block(g70)
    c: Weight(g73) = 1
    c: Equal(g73,g74)
    c: Equal(g73,g75)
    c: InternalAlignment(g73,g76)
    c: InternalAlignment(g74,g76)
    c: InternalAlignment(g75,g76)
    c: InternalAlignment(g77,g76)
    c: InternalAlignment(g78,g76)
    c: Weight(g79) = 1
    c: Equal(g79,g80)
    c: Equal(g79,g81)
    c: InternalAlignment(g79,g82)
    c: InternalAlignment(g80,g82)
    c: InternalAlignment(g81,g82)
    c: InternalAlignment(g83,g82)
    c: InternalAlignment(g84,g82)
    c: Block(g76)
    c: Block(g82)
    c: Coincident(g85,g76)
    c: Coincident(g85,g82)
    c: Vertical(g85)
    c: Coincident(g86,g76)
    c: Coincident(g86,g58)
    c: Coincident(g87,g58)
    c: Coincident(g87,g82)
    c: Weight(g88) = 1
    c: Equal(g88,g89)
    c: Equal(g88,g90)
    c: InternalAlignment(g88,g91)
    c: InternalAlignment(g89,g91)
    c: InternalAlignment(g90,g91)
    c: InternalAlignment(g92,g91)
    c: InternalAlignment(g93,g91)
    c: Weight(g94) = 1
    c: Equal(g94,g95)
    c: Equal(g94,g96)
    c: InternalAlignment(g94,g97)
    c: InternalAlignment(g95,g97)
    c: InternalAlignment(g96,g97)
    c: InternalAlignment(g98,g97)
    c: InternalAlignment(g99,g97)
    c: Block(g91)
    c: Block(g97)
    c: Coincident(g100,g91)
    c: Coincident(g100,g97)
    c: Vertical(g100)
    c: Coincident(g101,g91)
    c: Coincident(g101,g52)
    c: Coincident(g102,g52)
    c: Coincident(g102,g97)
    c: Weight(g103) = 1
    c: Equal(g103,g104)
    c: Equal(g103,g105)
    c: InternalAlignment(g103,g106)
    c: InternalAlignment(g104,g106)
    c: InternalAlignment(g105,g106)
    c: InternalAlignment(g107,g106)
    c: InternalAlignment(g108,g106)
    c: Weight(g109) = 1
    c: Equal(g109,g110)
    c: Equal(g109,g111)
    c: InternalAlignment(g109,g112)
    c: InternalAlignment(g110,g112)
    c: InternalAlignment(g111,g112)
    c: InternalAlignment(g113,g112)
    c: InternalAlignment(g114,g112)
    c: Block(g106)
    c: Block(g112)
    c: Coincident(g115,g106)
    c: Coincident(g115,g112)
    c: Vertical(g115)
    c: Coincident(g116,g112)
    c: Coincident(g116,g70)
    c: Coincident(g117,g70)
    c: Coincident(g117,g106)
    c: Weight(g118) = 1
    c: Equal(g118,g119)
    c: Equal(g118,g120)
    c: InternalAlignment(g118,g121)
    c: InternalAlignment(g119,g121)
    c: InternalAlignment(g120,g121)
    c: InternalAlignment(g122,g121)
    c: InternalAlignment(g123,g121)
    c: Weight(g124) = 1
    c: Equal(g124,g125)
    c: Equal(g124,g126)
    c: InternalAlignment(g124,g127)
    c: InternalAlignment(g125,g127)
    c: InternalAlignment(g126,g127)
    c: InternalAlignment(g128,g127)
    c: InternalAlignment(g129,g127)
    c: Block(g121)
    c: Block(g127)
    c: Coincident(g130,g121)
    c: Coincident(g130,g127)
    c: Vertical(g130)
    c: Coincident(g131,g127)
    c: Coincident(g131,g64)
    c: Coincident(g132,g64)
    c: Coincident(g132,g121)
    c: Weight(g133) = 1
    c: Equal(g133,g134)
    c: Equal(g133,g135)
    c: InternalAlignment(g133,g136)
    c: InternalAlignment(g134,g136)
    c: InternalAlignment(g135,g136)
    c: InternalAlignment(g137,g136)
    c: InternalAlignment(g138,g136)
    c: Weight(g139) = 1
    c: Equal(g139,g140)
    c: Equal(g139,g141)
    c: InternalAlignment(g139,g142)
    c: InternalAlignment(g140,g142)
    c: InternalAlignment(g141,g142)
    c: InternalAlignment(g143,g142)
    c: InternalAlignment(g144,g142)
    c: Weight(g145) = 1
    c: Equal(g145,g146)
    c: Equal(g145,g147)
    c: InternalAlignment(g145,g148)
    c: InternalAlignment(g146,g148)
    c: InternalAlignment(g147,g148)
    c: InternalAlignment(g149,g148)
    c: InternalAlignment(g150,g148)
    c: Weight(g151) = 1
    c: Equal(g151,g152)
    c: Equal(g151,g153)
    c: InternalAlignment(g151,g154)
    c: InternalAlignment(g152,g154)
    c: InternalAlignment(g153,g154)
    c: InternalAlignment(g155,g154)
    c: InternalAlignment(g156,g154)
    c: Block(g154)
    c: Block(g148)
    c: Block(g142)
    c: Block(g136)
    c: Coincident(g157,g31)
    c: Coincident(g157,g154)
    c: Coincident(g158,g154)
    c: Coincident(g158,g148)
    c: Horizontal(g158)
    c: Coincident(g159,g148)
    c: Coincident(g159,g31)
    c: Vertical(g159)
    c: Coincident(g160,g25)
    c: Coincident(g160,g142)
    c: Vertical(g160)
    c: Coincident(g161,g142)
    c: Coincident(g161,g136)
    c: Horizontal(g161)
    c: Coincident(g162,g136)
    c: Coincident(g162,g25)
    c: Weight(g163) = 1
    c: Equal(g163,g164)
    c: Equal(g163,g165)
    c: InternalAlignment(g163,g166)
    c: InternalAlignment(g164,g166)
    c: InternalAlignment(g165,g166)
    c: InternalAlignment(g167,g166)
    c: InternalAlignment(g168,g166)
    c: Weight(g169) = 1
    c: Equal(g169,g170)
    c: Equal(g169,g171)
    c: InternalAlignment(g169,g172)
    c: InternalAlignment(g170,g172)
    c: InternalAlignment(g171,g172)
    c: InternalAlignment(g173,g172)
    c: InternalAlignment(g174,g172)
    c: Weight(g175) = 1
    c: Equal(g175,g176)
    c: Equal(g175,g177)
    c: InternalAlignment(g175,g178)
    c: InternalAlignment(g176,g178)
    c: InternalAlignment(g177,g178)
    c: InternalAlignment(g179,g178)
    c: InternalAlignment(g180,g178)
    c: Weight(g181) = 1
    c: Equal(g181,g182)
    c: Equal(g181,g183)
    c: InternalAlignment(g181,g184)
    c: InternalAlignment(g182,g184)
    c: InternalAlignment(g183,g184)
    c: InternalAlignment(g185,g184)
    c: InternalAlignment(g186,g184)
    c: Block(g184)
    c: Block(g178)
    c: Block(g172)
    c: Block(g166)
    c: Coincident(g187,g184)
    c: Coincident(g187,g178)
    c: Horizontal(g187)
    c: Coincident(g188,g178)
    c: Coincident(g188,g13)
    c: Vertical(g188)
    c: Coincident(g189,g19)
    c: Coincident(g189,g172)
    c: Vertical(g189)
    c: Coincident(g190,g172)
    c: Coincident(g190,g166)
    c: Horizontal(g190)
    c: Coincident(g191,g166)
    c: Coincident(g191,g19)
    c: Coincident(g192,g13)
    c: Weight(g193) = 1
    c: Equal(g193,g194)
    c: Equal(g193,g195)
    c: InternalAlignment(g193,g196)
    c: InternalAlignment(g194,g196)
    c: InternalAlignment(g195,g196)
    c: InternalAlignment(g197,g196)
    c: InternalAlignment(g198,g196)
    c: Weight(g199) = 1
    c: Equal(g199,g200)
    c: Equal(g199,g201)
    c: InternalAlignment(g199,g202)
    c: InternalAlignment(g200,g202)
    c: InternalAlignment(g201,g202)
    c: InternalAlignment(g203,g202)
    c: InternalAlignment(g204,g202)
    c: Block(g202)
    c: Block(g196)
    c: Coincident(g205,g202)
    c: Coincident(g205,g37)
    c: Coincident(g206,g37)
    c: Coincident(g206,g196)
    c: Coincident(g207,g196)
    c: Coincident(g207,g202)
    c: Vertical(g207)
    c: Weight(g208) = 1
    c: Equal(g208,g209)
    c: Equal(g208,g210)
    c: InternalAlignment(g208,g211)
    c: InternalAlignment(g209,g211)
    c: InternalAlignment(g210,g211)
    c: InternalAlignment(g212,g211)
    c: InternalAlignment(g213,g211)
    c: Weight(g214) = 1
    c: Equal(g214,g215)
    c: Equal(g214,g216)
    c: InternalAlignment(g214,g217)
    c: InternalAlignment(g215,g217)
    c: InternalAlignment(g216,g217)
    c: InternalAlignment(g218,g217)
    c: InternalAlignment(g219,g217)
    c: Block(g217)
    c: Block(g211)
    c: Coincident(g220,g211)
    c: Coincident(g220,g43)
    c: Coincident(g221,g43)
    c: Coincident(g221,g217)
    c: Coincident(g222,g217)
    c: Coincident(g222,g211)
    c: Vertical(g222)
    c: Horizontal(g223)
    c: Block(g223)
    c: Vertical(g224)
    c: Block(g224)
    c: Block(g225)
    c: Weight(g226) = 1
    c: Equal(g226,g227)
    c: Equal(g226,g228)
    c: InternalAlignment(g226,g229)
    c: InternalAlignment(g227,g229)
    c: InternalAlignment(g228,g229)
    c: InternalAlignment(g230,g229)
    c: InternalAlignment(g231,g229)
    c: Weight(g232) = 1
    c: Equal(g232,g233)
    c: Equal(g232,g234)
    c: InternalAlignment(g232,g235)
    c: InternalAlignment(g233,g235)
    c: InternalAlignment(g234,g235)
    c: InternalAlignment(g236,g235)
    c: InternalAlignment(g237,g235)
    c: Weight(g238) = 1
    c: Equal(g238,g239)
    c: Equal(g238,g240)
    c: InternalAlignment(g238,g241)
    c: InternalAlignment(g239,g241)
    c: InternalAlignment(g240,g241)
    c: InternalAlignment(g242,g241)
    c: InternalAlignment(g243,g241)
    c: Weight(g244) = 1
    c: Equal(g244,g245)
    c: Equal(g244,g246)
    c: InternalAlignment(g244,g247)
    c: InternalAlignment(g245,g247)
    c: InternalAlignment(g246,g247)
    c: InternalAlignment(g248,g247)
    c: InternalAlignment(g249,g247)
    c: Block(g229)
    c: Block(g235)
    c: Block(g241)
    c: Block(g247)
    c: Coincident(g250,g235)
    c: Coincident(g250,g229)
    c: Horizontal(g250)
    c: Block(g192)
    c: Weight(g251) = 1
    c: Equal(g251,g252)
    c: Equal(g251,g253)
    c: InternalAlignment(g251,g254)
    c: InternalAlignment(g252,g254)
    c: InternalAlignment(g253,g254)
    c: InternalAlignment(g255,g254)
    c: InternalAlignment(g256,g254)
    c: Weight(g257) = 1
    c: Equal(g257,g258)
    c: Equal(g257,g259)
    c: InternalAlignment(g257,g260)
    c: InternalAlignment(g258,g260)
    c: InternalAlignment(g259,g260)
    c: InternalAlignment(g261,g260)
    c: InternalAlignment(g262,g260)
    c: Block(g254)
    c: Block(g260)
    c: Coincident(g263,g254)
    c: Coincident(g263,g260)
    c: Weight(g264) = 1
    c: Equal(g264,g265)
    c: Equal(g264,g266)
    c: InternalAlignment(g264,g267)
    c: InternalAlignment(g265,g267)
    c: InternalAlignment(g266,g267)
    c: InternalAlignment(g268,g267)
    c: InternalAlignment(g269,g267)
    c: Weight(g270) = 1
    c: Equal(g270,g271)
    c: Equal(g270,g272)
    c: InternalAlignment(g270,g273)
    c: InternalAlignment(g271,g273)
    c: InternalAlignment(g272,g273)
    c: InternalAlignment(g274,g273)
    c: InternalAlignment(g275,g273)
    c: Weight(g276) = 1
    c: Equal(g276,g277)
    c: Equal(g276,g278)
    c: InternalAlignment(g276,g279)
    c: InternalAlignment(g277,g279)
    c: InternalAlignment(g278,g279)
    c: InternalAlignment(g280,g279)
    c: InternalAlignment(g281,g279)
    c: Block(g279)
    c: Block(g273)
    c: Block(g267)
    c: Coincident(g282,g273)
    c: Coincident(g282,g267)
    c: Coincident(g283,g267)
    c: Coincident(g283,g279)
    c: Vertical(g283)
    c: Coincident(g284,g279)
    c: Coincident(g284,g273)
    c: Horizontal(g284)
    c: Weight(g285) = 1
    c: Equal(g285,g286)
    c: InternalAlignment(g285,g287)
    c: InternalAlignment(g286,g287)
    c: InternalAlignment(g288,g287)
    c: InternalAlignment(g289,g287)
    c: Weight(g290) = 1
    c: InternalAlignment(g291,g293)
    c: InternalAlignment(g292,g293)
    c: InternalAlignment(g294,g293)
    c: InternalAlignment(g295,g293)
    c: Weight(g296) = 1
    c: Equal(g296,g297)
    c: Equal(g296,g298)
    c: InternalAlignment(g296,g299)
    c: InternalAlignment(g297,g299)
    c: InternalAlignment(g298,g299)
    c: InternalAlignment(g300,g299)
    c: InternalAlignment(g301,g299)
    c: Equal(g302,g303)
    c: Equal(g302,g304)
    c: InternalAlignment(g302,g305)
    c: InternalAlignment(g303,g305)
    c: InternalAlignment(g304,g305)
    c: InternalAlignment(g306,g305)
    c: InternalAlignment(g307,g305)
    c: Block(g293)
    c: Block(g299)
    c: Block(g305)
    c: Block(g287)
    c: Coincident(g308,g287)
    c: Coincident(g308,g293)
    c: Horizontal(g308)
    c: Coincident(g309,g293)
    c: Coincident(g309,g299)
    c: Vertical(g309)
    c: Coincident(g310,g299)
    c: Coincident(g310,g305)
    c: Horizontal(g310)
    c: Coincident(g311,g305)
    c: Coincident(g311,g287)
    c: Weight(g312) = 1
    c: Equal(g312,g313)
    c: Equal(g312,g314)
    c: InternalAlignment(g312,g315)
    c: InternalAlignment(g313,g315)
    c: InternalAlignment(g314,g315)
    c: InternalAlignment(g316,g315)
    c: InternalAlignment(g317,g315)
    c: Weight(g318) = 1
    c: Equal(g318,g319)
    c: Equal(g318,g320)
    c: InternalAlignment(g318,g321)
    c: InternalAlignment(g319,g321)
    c: InternalAlignment(g320,g321)
    c: InternalAlignment(g322,g321)
    c: InternalAlignment(g323,g321)
    c: Weight(g324) = 1
    c: Equal(g324,g325)
    c: Equal(g324,g326)
    c: InternalAlignment(g324,g327)
    c: InternalAlignment(g325,g327)
    c: InternalAlignment(g326,g327)
    c: InternalAlignment(g328,g327)
    c: InternalAlignment(g329,g327)
    c: Block(g327)
    c: Block(g321)
    c: Block(g315)
    c: Coincident(g330,g327)
    c: Coincident(g330,g321)
    c: Horizontal(g330)
    c: Coincident(g331,g321)
    c: Coincident(g331,g315)
    c: Vertical(g331)
    c: Coincident(g332,g315)
    c: Coincident(g332,g327)
    c: InternalAlignment(g333,g334)
    c: InternalAlignment(g335,g334)
    c: InternalAlignment(g336,g334)
    c: Block(g334)
    c: Equal(g337,g338)
    c: Equal(g337,g339)
    c: InternalAlignment(g337,g340)
    c: InternalAlignment(g338,g340)
    c: InternalAlignment(g339,g340)
    c: InternalAlignment(g341,g340)
    c: InternalAlignment(g342,g340)
    c: Block(g340)
    c: Coincident(g343,g334)
    c: Horizontal(g343)
    c: Block(g343)
    c: Coincident(g344,g334)
    c: Coincident(g344,g260)
    c: Vertical(g344)
    c: Coincident(g345,g340)
    c: Coincident(g345,g254)
    c: Vertical(g345)
    c: Coincident(g347,g5)
    c: Coincident(g348,g5)
    c: Block(g346)
    c: Block(g5)
    c: Block(g348)
    c: Block(g347)
    c: Distance(g344) = 119.89
FEATURE [Sketcher::SketchObject] Sketch001
  FullyConstrained = true
  MapMode = 4
  Placement = pos=(0,0,0) rot=(0.57735,0.57735,0.57735;2.0944rad)
  Support = -> [Sketch]
  sketch-geometry (46):
    g0: BSplineCurve PolesCount=3 KnotsCount=2 Degree=2 IsPeriodic=0
    g1: ArcOfCircle CenterX=73.1223 CenterY=-32.291 CenterZ=0 NormalX=0 NormalY=0 NormalZ=1 AngleXU=0 Radius=13 StartAngle=5.92268 EndAngle=9.06428
    g2: ArcOfCircle CenterX=66.7816 CenterY=-49.1439 CenterZ=0 NormalX=0 NormalY=0 NormalZ=1 AngleXU=0 Radius=13 StartAngle=2.78068 EndAngle=5.92131
    g3: ArcOfCircle CenterX=55.9263 CenterY=-78.1807 CenterZ=0 NormalX=0 NormalY=0 NormalZ=1 AngleXU=0 Radius=13 StartAngle=5.92268 EndAngle=9.06428
    g4: ArcOfCircle CenterX=49.5884 CenterY=-95.0342 CenterZ=0 NormalX=0 NormalY=0 NormalZ=1 AngleXU=0 Radius=13 StartAngle=2.78068 EndAngle=5.92131
    g5: ArcOfCircle CenterX=38.7206 CenterY=-124.067 CenterZ=0 NormalX=0 NormalY=0 NormalZ=1 AngleXU=0 Radius=13 StartAngle=5.92268 EndAngle=9.06428
    g6: ArcOfCircle CenterX=32.3875 CenterY=-140.92 CenterZ=0 NormalX=0 NormalY=0 NormalZ=1 AngleXU=0 Radius=13 StartAngle=2.78068 EndAngle=5.92131
    g7: ArcOfCircle CenterX=21.4715 CenterY=-169.934 CenterZ=0 NormalX=0 NormalY=0 NormalZ=1 AngleXU=0 Radius=13 StartAngle=5.92268 EndAngle=9.06428
    g8: ArcOfCircle CenterX=15.1336 CenterY=-186.787 CenterZ=0 NormalX=0 NormalY=0 NormalZ=1 AngleXU=0 Radius=13 StartAngle=2.78068 EndAngle=5.92131
    g9-g12: Circle x4 (B-spline internal-alignment scaffolding for g13; pole/knot coordinates omitted)
    g13: BSplineCurve PolesCount=4 KnotsCount=2 Degree=3 IsPeriodic=0
    g14: GeomPoint X=28.8094 Y=-19.0875 Z=0
    g15: GeomPoint X=47.0443 Y=-50.4712 Z=0
    g16: Circle CenterX=53.5586 CenterY=-23.2695 CenterZ=0 NormalX=0 NormalY=0 NormalZ=1 AngleXU=0 Radius=3.24518
    g17: Circle CenterX=-195.441 CenterY=-127.082 CenterZ=0 NormalX=0 NormalY=0 NormalZ=1 AngleXU=0 Radius=1
    g18: Circle CenterX=-8.24091 CenterY=-197.481 CenterZ=0 NormalX=0 NormalY=0 NormalZ=1 AngleXU=0 Radius=1
    g19: Circle CenterX=12.8789 CenterY=-141.321 CenterZ=0 NormalX=0 NormalY=0 NormalZ=1 AngleXU=0 Radius=1
    g20: BSplineCurve PolesCount=3 KnotsCount=2 Degree=2 IsPeriodic=0
    g21: GeomPoint X=-195.441 Y=-127.082 Z=0
    g22: GeomPoint X=12.8789 Y=-141.321 Z=0
    g23: Circle CenterX=-12.8016 CenterY=-179.036 CenterZ=0 NormalX=0 NormalY=0 NormalZ=1 AngleXU=0 Radius=10.5072
    g24: Circle CenterX=0.933922 CenterY=-166.43 CenterZ=0 NormalX=0 NormalY=0 NormalZ=1 AngleXU=0 Radius=3.26661
    g25: Circle CenterX=-33.5518 CenterY=-176.44 CenterZ=0 NormalX=0 NormalY=0 NormalZ=1 AngleXU=0 Radius=5.64388
    g26: Circle CenterX=-47.2366 CenterY=-173.859 CenterZ=0 NormalX=0 NormalY=0 NormalZ=1 AngleXU=0 Radius=3.01653
    g27: Circle CenterX=-56.2595 CenterY=-171.456 CenterZ=0 NormalX=0 NormalY=0 NormalZ=1 AngleXU=0 Radius=2.12826
    g28: ArcOfCircle CenterX=51.2151 CenterY=-198.473 CenterZ=0 NormalX=0 NormalY=0 NormalZ=1 AngleXU=0 Radius=20 StartAngle=2.78189 EndAngle=4.35269
    g29: LineSegment StartX=32.4951 StartY=-191.433 StartZ=0 EndX=94.6578 EndY=-26.1352 EndZ=0
    g30: LineSegment StartX=43.1192 StartY=-220.001 StartZ=0 EndX=-196.497 EndY=-129.89 EndZ=0
    g31: LineSegment StartX=43.1192 StartY=-220.001 StartZ=0 EndX=44.1752 EndY=-217.193 EndZ=0
    g32: LineSegment StartX=117.223 StartY=-19.0875 StartZ=0 EndX=117.223 EndY=-16.0875 EndZ=0
    g33: LineSegment StartX=117.223 StartY=-16.0875 StartZ=0 EndX=17.2232 EndY=-16.0875 EndZ=0
    g34: LineSegment StartX=17.2232 StartY=-16.0875 StartZ=0 EndX=17.2232 EndY=-19.0875 EndZ=0
    g35: LineSegment StartX=28.8094 StartY=-19.0875 StartZ=0 EndX=17.2232 EndY=-19.0875 EndZ=0
    g36: LineSegment StartX=47.0443 StartY=-50.4712 StartZ=0 EndX=12.8789 EndY=-141.321 EndZ=0
    g37: LineSegment StartX=-195.441 StartY=-127.082 StartZ=0 EndX=-196.497 EndY=-129.89 EndZ=0
    g38: LineSegment StartX=85.2866 StartY=-36.8766 StartZ=0 EndX=78.9396 EndY=-53.7463 EndZ=0
    g39: LineSegment StartX=60.9579 StartY=-27.7053 StartZ=0 EndX=54.6191 EndY=-44.5532 EndZ=0
    g40: LineSegment StartX=68.0907 StartY=-82.7664 StartZ=0 EndX=61.7465 EndY=-99.6365 EndZ=0
    g41: LineSegment StartX=43.7619 StartY=-73.595 StartZ=0 EndX=37.426 EndY=-90.4435 EndZ=0
    g42: LineSegment StartX=50.885 StartY=-128.652 StartZ=0 EndX=44.5456 EndY=-145.522 EndZ=0
    g43: LineSegment StartX=26.5562 StartY=-119.481 StartZ=0 EndX=20.2251 EndY=-136.329 EndZ=0
    g44: LineSegment StartX=9.3071 StartY=-165.349 StartZ=0 EndX=2.97115 EndY=-182.197 EndZ=0
    g45: LineSegment StartX=33.6358 StartY=-174.52 StartZ=0 EndX=27.2917 EndY=-191.39 EndZ=0
  constraints (71):
    c: Block(g0)
    c: Block(g1)
    c: Block(g2)
    c: Block(g4)
    c: Block(g3)
    c: Block(g6)
    c: Block(g5)
    c: Block(g8)
    c: Block(g7)
    c: Weight(g9) = 1
    c: Equal(g9,g10)
    c: Equal(g9,g11)
    c: Equal(g9,g12)
    c: InternalAlignment(g9-g12 -> g13) x4
    c: InternalAlignment(g14,g13)
    c: InternalAlignment(g15,g13)
    c: Block(g16)
    c: Weight(g17) = 1
    c: Equal(g17,g18)
    c: Equal(g17,g19)
    c: InternalAlignment(g17,g20)
    c: InternalAlignment(g18,g20)
    c: InternalAlignment(g19,g20)
    c: InternalAlignment(g21,g20)
    c: InternalAlignment(g22,g20)
    c: Block(g20)
    c: Block(g23)
    c: Block(g24)
    c: Block(g25)
    c: Block(g26)
    c: Block(g27)
    c: Block(g28)
    c: Coincident(g29,g28)
    c: Coincident(g29,g0)
    c: Block(g13)
    c: Coincident(g31,g30)
    c: Coincident(g31,g28)
    c: Block(g31)
    c: Coincident(g32,g0)
    c: Vertical(g32)
    c: Coincident(g33,g32)
    c: Horizontal(g33)
    c: Coincident(g34,g33)
    c: Vertical(g34)
    c: Block(g33)
    c: Coincident(g35,g13)
    c: Coincident(g35,g34)
    c: Horizontal(g35)
    c: Coincident(g36,g13)
    c: Coincident(g36,g20)
    c: Coincident(g37,g20)
    c: Coincident(g37,g30)
    c: Block(g30)
    c: Coincident(g38,g1)
    c: Coincident(g38,g2)
    c: Coincident(g39,g1)
    c: Coincident(g39,g2)
    c: Coincident(g40,g3)
    c: Coincident(g40,g4)
    c: Coincident(g41,g3)
    c: Coincident(g41,g4)
    c: Coincident(g42,g5)
    c: Coincident(g42,g6)
    c: Coincident(g43,g5)
    c: Coincident(g43,g6)
    c: Coincident(g44,g7)
    c: Coincident(g44,g8)
    c: Coincident(g45,g7)
    c: Coincident(g45,g8)
    c: Distance(g30) = 256
    c: Distance(g33) = 100
FEATURE [Part::Extrusion] Extrude002
  Base = -> Sketch001
  Dir = (1,0,0)
  DirMode = 2
  FaceMakerClass = Part::FaceMakerBullseye
  LengthFwd = 8
  LengthRev = 0
  Solid = true
  Symmetric = false
FEATURE [Sketcher::SketchObject] Sketch002
  FullyConstrained = true
  sketch-geometry (20):
    g0: LineSegment StartX=-2.77179 StartY=-200.304 StartZ=0 EndX=5.22821 EndY=-200.304 EndZ=0
    g1: LineSegment StartX=5.22821 StartY=-200.304 StartZ=0 EndX=5.22821 EndY=-197.304 EndZ=0
    g2: LineSegment StartX=-2.77179 StartY=-200.304 StartZ=0 EndX=-2.77179 EndY=-197.304 EndZ=0
    g3: LineSegment StartX=5.22821 StartY=-197.304 StartZ=0 EndX=8.22821 EndY=-197.304 EndZ=0
    g4: LineSegment StartX=-2.77179 StartY=-197.304 StartZ=0 EndX=-5.77179 EndY=-197.304 EndZ=0
    g5: LineSegment StartX=19.2282 StartY=-203.304 StartZ=0 EndX=19.2282 EndY=-206.304 EndZ=0
    g6: LineSegment StartX=-16.7718 StartY=-203.304 StartZ=0 EndX=-16.7718 EndY=-206.304 EndZ=0
    g7: LineSegment StartX=-16.7718 StartY=-206.304 StartZ=0 EndX=19.2282 EndY=-206.304 EndZ=0
    g8: Circle CenterX=-16.7718 CenterY=-203.304 CenterZ=0 NormalX=0 NormalY=0 NormalZ=1 AngleXU=0 Radius=1
    g9: Circle CenterX=-5.77179 CenterY=-203.304 CenterZ=0 NormalX=0 NormalY=0 NormalZ=1 AngleXU=0 Radius=1
    g10: Circle CenterX=-5.77179 CenterY=-197.304 CenterZ=0 NormalX=0 NormalY=0 NormalZ=1 AngleXU=0 Radius=1
    g11: BSplineCurve PolesCount=3 KnotsCount=2 Degree=2 IsPeriodic=0
    g12: GeomPoint X=-16.7718 Y=-203.304 Z=0
    g13: GeomPoint X=-5.77179 Y=-197.304 Z=0
    g14: Circle CenterX=19.2282 CenterY=-203.304 CenterZ=0 NormalX=0 NormalY=0 NormalZ=1 AngleXU=0 Radius=1
    g15: Circle CenterX=8.22821 CenterY=-203.304 CenterZ=0 NormalX=0 NormalY=0 NormalZ=1 AngleXU=0 Radius=1
    g16: Circle CenterX=8.22821 CenterY=-197.304 CenterZ=0 NormalX=0 NormalY=0 NormalZ=1 AngleXU=0 Radius=1
    g17: BSplineCurve PolesCount=3 KnotsCount=2 Degree=2 IsPeriodic=0
    g18: GeomPoint X=19.2282 Y=-203.304 Z=0
    g19: GeomPoint X=8.22821 Y=-197.304 Z=0
  constraints (41):
    c: Horizontal(g0)
    c: Distance(g0) = 8
    c: Coincident(g1,g0)
    c: Vertical(g1)
    c: Distance(g1) = 3
    c: Coincident(g2,g0)
    c: Vertical(g2)
    c: Distance(g2) = 3
    c: Coincident(g3,g1)
    c: Horizontal(g3)
    c: Distance(g3) = 3
    c: Coincident(g4,g2)
    c: Horizontal(g4)
    c: Distance(g4) = 3
    c: Vertical(g5)
    c: Vertical(g6)
    c: Coincident(g7,g6)
    c: Coincident(g7,g5)
    c: Weight(g8) = 1
    c: Equal(g8,g9)
    c: Equal(g8,g10)
    c: Coincident(g11,g4)
    c: InternalAlignment(g8,g11)
    c: InternalAlignment(g9,g11)
    c: InternalAlignment(g10,g11)
    c: InternalAlignment(g12,g11)
    c: InternalAlignment(g13,g11)
    c: Coincident(g17,g5)
    c: Weight(g14) = 1
    c: Equal(g14,g15)
    c: Equal(g14,g16)
    c: Coincident(g17,g3)
    c: InternalAlignment(g14,g17)
    c: InternalAlignment(g15,g17)
    c: InternalAlignment(g16,g17)
    c: InternalAlignment(g18,g17)
    c: InternalAlignment(g19,g17)
    c: Block(g7)
    c: Block(g17)
    c: Block(g11)
    c: Block(g6)
FEATURE [Part::Extrusion] Extrude003
  Base = -> Sketch002
  Dir = (0,0,1)
  DirMode = 2
  FaceMakerClass = Part::FaceMakerBullseye
  LengthFwd = 260
  LengthRev = 0
  Solid = true
  Symmetric = false
FEATURE [Part::Extrusion] Extrude
  Base = -> Sketch
  Dir = (0,0,1)
  DirMode = 2
  FaceMakerClass = Part::FaceMakerBullseye
  LengthFwd = 14
  LengthRev = 0
  Solid = true
  Symmetric = false
FEATURE [Sketcher::SketchObject] Sketch003
  FullyConstrained = false
  sketch-geometry (373):
    g0: LineSegment StartX=-42.9272 StartY=136.221 StartZ=0 EndX=-42.9272 EndY=-103.779 EndZ=0
    g1: LineSegment StartX=407.073 StartY=136.221 StartZ=0 EndX=407.073 EndY=-103.779 EndZ=0
    g2: ArcOfCircle CenterX=-26.9272 CenterY=-83.7794 CenterZ=0 NormalX=0 NormalY=0 NormalZ=1 AngleXU=0 Radius=8 StartAngle=3.14159 EndAngle=6.28319
    g3: ArcOfCircle CenterX=391.073 CenterY=-83.7794 CenterZ=0 NormalX=0 NormalY=0 NormalZ=1 AngleXU=0 Radius=8 StartAngle=3.14159 EndAngle=6.28319
    g4: Circle CenterX=175.022 CenterY=27.0628 CenterZ=0 NormalX=0 NormalY=0 NormalZ=1 AngleXU=0 Radius=1
    g5: Circle CenterX=179.022 CenterY=24.8665 CenterZ=0 NormalX=0 NormalY=0 NormalZ=1 AngleXU=0 Radius=1
    g6: Circle CenterX=179.022 CenterY=27.0628 CenterZ=0 NormalX=0 NormalY=0 NormalZ=1 AngleXU=0 Radius=1
    g7: BSplineCurve PolesCount=3 KnotsCount=2 Degree=2 IsPeriodic=0
    g8: GeomPoint X=175.022 Y=27.0628 Z=0
    g9: GeomPoint X=179.022 Y=27.0628 Z=0
    g10: Circle CenterX=189.124 CenterY=27.0628 CenterZ=0 NormalX=0 NormalY=0 NormalZ=1 AngleXU=0 Radius=1
    g11: Circle CenterX=185.124 CenterY=24.8665 CenterZ=0 NormalX=0 NormalY=0 NormalZ=1 AngleXU=0 Radius=1
    g12: Circle CenterX=185.124 CenterY=27.0628 CenterZ=0 NormalX=0 NormalY=0 NormalZ=1 AngleXU=0 Radius=1
    g13: BSplineCurve PolesCount=3 KnotsCount=2 Degree=2 IsPeriodic=0
    g14: GeomPoint X=189.124 Y=27.0628 Z=0
    g15: GeomPoint X=185.124 Y=27.0628 Z=0
    g16: Circle CenterX=175.022 CenterY=5.37834 CenterZ=0 NormalX=0 NormalY=0 NormalZ=1 AngleXU=0 Radius=1
    g17: Circle CenterX=179.022 CenterY=7.57463 CenterZ=0 NormalX=0 NormalY=0 NormalZ=1 AngleXU=0 Radius=1
    g18: Circle CenterX=179.022 CenterY=5.34704 CenterZ=0 NormalX=0 NormalY=0 NormalZ=1 AngleXU=0 Radius=1
    g19: BSplineCurve PolesCount=3 KnotsCount=2 Degree=2 IsPeriodic=0
    g20: GeomPoint X=175.022 Y=5.37834 Z=0
    g21: GeomPoint X=179.022 Y=5.34704 Z=0
    g22: Circle CenterX=189.124 CenterY=5.37834 CenterZ=0 NormalX=0 NormalY=0 NormalZ=1 AngleXU=0 Radius=1
    g23: Circle CenterX=185.124 CenterY=7.57463 CenterZ=0 NormalX=0 NormalY=0 NormalZ=1 AngleXU=0 Radius=1
    g24: Circle CenterX=185.124 CenterY=5.34704 CenterZ=0 NormalX=0 NormalY=0 NormalZ=1 AngleXU=0 Radius=1
    g25: BSplineCurve PolesCount=3 KnotsCount=2 Degree=2 IsPeriodic=0
    g26: GeomPoint X=189.124 Y=5.37834 Z=0
    g27: GeomPoint X=185.124 Y=5.34704 Z=0
    g28: Circle CenterX=165.871 CenterY=18.1458 CenterZ=0 NormalX=0 NormalY=0 NormalZ=1 AngleXU=0 Radius=1
    g29: Circle CenterX=169.377 CenterY=16.2206 CenterZ=0 NormalX=0 NormalY=0 NormalZ=1 AngleXU=0 Radius=1
    g30: Circle CenterX=165.871 CenterY=14.2954 CenterZ=0 NormalX=0 NormalY=0 NormalZ=1 AngleXU=0 Radius=1
    g31: BSplineCurve PolesCount=3 KnotsCount=2 Degree=2 IsPeriodic=0
    g32: GeomPoint X=165.871 Y=18.1458 Z=0
    g33: GeomPoint X=165.871 Y=14.2954 Z=0
    g34: Circle CenterX=198.275 CenterY=18.1458 CenterZ=0 NormalX=0 NormalY=0 NormalZ=1 AngleXU=0 Radius=1
    g35: Circle CenterX=194.768 CenterY=16.2206 CenterZ=0 NormalX=0 NormalY=0 NormalZ=1 AngleXU=0 Radius=1
    g36: Circle CenterX=198.275 CenterY=14.2954 CenterZ=0 NormalX=0 NormalY=0 NormalZ=1 AngleXU=0 Radius=1
    g37: BSplineCurve PolesCount=3 KnotsCount=2 Degree=2 IsPeriodic=0
    g38: GeomPoint X=198.275 Y=18.1458 Z=0
    g39: GeomPoint X=198.275 Y=14.2954 Z=0
    g40: LineSegment StartX=407.073 StartY=-103.779 StartZ=0 EndX=-42.9272 EndY=-103.779 EndZ=0
    g41: LineSegment StartX=407.073 StartY=136.221 StartZ=0 EndX=-42.9272 EndY=136.221 EndZ=0
    g42: Circle CenterX=125.607 CenterY=54.1951 CenterZ=0 NormalX=0 NormalY=0 NormalZ=1 AngleXU=0 Radius=1
    g43: Circle CenterX=139.632 CenterY=46.4944 CenterZ=0 NormalX=0 NormalY=0 NormalZ=1 AngleXU=0 Radius=1
    g44: Circle CenterX=127.326 CenterY=56.7187 CenterZ=0 NormalX=0 NormalY=0 NormalZ=1 AngleXU=0 Radius=1
    g45: BSplineCurve PolesCount=3 KnotsCount=2 Degree=2 IsPeriodic=0
    g46: GeomPoint X=125.607 Y=54.1951 Z=0
    g47: GeomPoint X=127.326 Y=56.7187 Z=0
    g48: Circle CenterX=236.821 CenterY=56.7187 CenterZ=0 NormalX=0 NormalY=0 NormalZ=1 AngleXU=0 Radius=1
    g49: Circle CenterX=224.513 CenterY=46.4944 CenterZ=0 NormalX=0 NormalY=0 NormalZ=1 AngleXU=0 Radius=1
    g50: Circle CenterX=238.538 CenterY=54.1951 CenterZ=0 NormalX=0 NormalY=0 NormalZ=1 AngleXU=0 Radius=1
    g51: BSplineCurve PolesCount=3 KnotsCount=2 Degree=2 IsPeriodic=0
    g52: GeomPoint X=236.821 Y=56.7187 Z=0
    g53: GeomPoint X=238.538 Y=54.1951 Z=0
    g54: Circle CenterX=238.538 CenterY=-21.7539 CenterZ=0 NormalX=0 NormalY=0 NormalZ=1 AngleXU=0 Radius=1
    g55: Circle CenterX=224.513 CenterY=-14.0532 CenterZ=0 NormalX=0 NormalY=0 NormalZ=1 AngleXU=0 Radius=1
    g56: Circle CenterX=236.821 CenterY=-24.2775 CenterZ=0 NormalX=0 NormalY=0 NormalZ=1 AngleXU=0 Radius=1
    g57: BSplineCurve PolesCount=3 KnotsCount=2 Degree=2 IsPeriodic=0
    g58: GeomPoint X=238.538 Y=-21.7539 Z=0
    g59: GeomPoint X=236.821 Y=-24.2775 Z=0
    g60: Circle CenterX=125.607 CenterY=-21.7539 CenterZ=0 NormalX=0 NormalY=0 NormalZ=1 AngleXU=0 Radius=1
    g61: Circle CenterX=139.632 CenterY=-14.0532 CenterZ=0 NormalX=0 NormalY=0 NormalZ=1 AngleXU=0 Radius=1
    g62: Circle CenterX=127.325 CenterY=-24.2775 CenterZ=0 NormalX=0 NormalY=0 NormalZ=1 AngleXU=0 Radius=1
    g63: BSplineCurve PolesCount=3 KnotsCount=2 Degree=2 IsPeriodic=0
    g64: GeomPoint X=125.607 Y=-21.7539 Z=0
    g65: GeomPoint X=127.325 Y=-24.2775 Z=0
    g66: Circle CenterX=302.996 CenterY=111.695 CenterZ=0 NormalX=0 NormalY=0 NormalZ=1 AngleXU=0 Radius=1
    g67: Circle CenterX=306.073 CenterY=114.251 CenterZ=0 NormalX=0 NormalY=0 NormalZ=1 AngleXU=0 Radius=1
    g68: Circle CenterX=306.073 CenterY=110.251 CenterZ=0 NormalX=0 NormalY=0 NormalZ=1 AngleXU=0 Radius=1
    g69: BSplineCurve PolesCount=3 KnotsCount=2 Degree=2 IsPeriodic=0
    g70: GeomPoint X=302.996 Y=111.695 Z=0
    g71: GeomPoint X=306.073 Y=110.251 Z=0
    g72: Circle CenterX=306.073 CenterY=95.2763 CenterZ=0 NormalX=0 NormalY=0 NormalZ=1 AngleXU=0 Radius=1
    g73: Circle CenterX=306.073 CenterY=91.2763 CenterZ=0 NormalX=0 NormalY=0 NormalZ=1 AngleXU=0 Radius=1
    g74: Circle CenterX=302.567 CenterY=89.3511 CenterZ=0 NormalX=0 NormalY=0 NormalZ=1 AngleXU=0 Radius=1
    g75: BSplineCurve PolesCount=3 KnotsCount=2 Degree=2 IsPeriodic=0
    g76: GeomPoint X=306.073 Y=95.2763 Z=0
    g77: GeomPoint X=302.567 Y=89.3511 Z=0
    g78: LineSegment StartX=306.073 StartY=110.251 StartZ=0 EndX=306.073 EndY=95.2763 EndZ=0
    g79: LineSegment StartX=302.996 StartY=111.695 StartZ=0 EndX=236.821 EndY=56.7187 EndZ=0
    g80: LineSegment StartX=238.538 StartY=54.1951 StartZ=0 EndX=302.567 EndY=89.3511 EndZ=0
    g81: Circle CenterX=61.1496 CenterY=111.695 CenterZ=0 NormalX=0 NormalY=0 NormalZ=1 AngleXU=0 Radius=1
    g82: Circle CenterX=58.0728 CenterY=114.251 CenterZ=0 NormalX=0 NormalY=0 NormalZ=1 AngleXU=0 Radius=1
    g83: Circle CenterX=58.0728 CenterY=110.251 CenterZ=0 NormalX=0 NormalY=0 NormalZ=1 AngleXU=0 Radius=1
    g84: BSplineCurve PolesCount=3 KnotsCount=2 Degree=2 IsPeriodic=0
    g85: GeomPoint X=61.1496 Y=111.695 Z=0
    g86: GeomPoint X=58.0728 Y=110.251 Z=0
    g87: Circle CenterX=61.5791 CenterY=89.3511 CenterZ=0 NormalX=0 NormalY=0 NormalZ=1 AngleXU=0 Radius=1
    g88: Circle CenterX=58.0728 CenterY=91.2763 CenterZ=0 NormalX=0 NormalY=0 NormalZ=1 AngleXU=0 Radius=1
    g89: Circle CenterX=58.0728 CenterY=95.2763 CenterZ=0 NormalX=0 NormalY=0 NormalZ=1 AngleXU=0 Radius=1
    g90: BSplineCurve PolesCount=3 KnotsCount=2 Degree=2 IsPeriodic=0
    g91: GeomPoint X=61.5791 Y=89.3511 Z=0
    g92: GeomPoint X=58.0728 Y=95.2763 Z=0
    g93: LineSegment StartX=58.0728 StartY=110.251 StartZ=0 EndX=58.0728 EndY=95.2763 EndZ=0
    g94: LineSegment StartX=61.1496 StartY=111.695 StartZ=0 EndX=127.326 EndY=56.7187 EndZ=0
    g95: LineSegment StartX=125.607 StartY=54.1951 StartZ=0 EndX=61.5791 EndY=89.3511 EndZ=0
    g96: Circle CenterX=61.5791 CenterY=-56.9099 CenterZ=0 NormalX=0 NormalY=0 NormalZ=1 AngleXU=0 Radius=1
    g97: Circle CenterX=58.0728 CenterY=-58.8351 CenterZ=0 NormalX=0 NormalY=0 NormalZ=1 AngleXU=0 Radius=1
    g98: Circle CenterX=58.0728 CenterY=-62.8351 CenterZ=0 NormalX=0 NormalY=0 NormalZ=1 AngleXU=0 Radius=1
    g99: BSplineCurve PolesCount=3 KnotsCount=2 Degree=2 IsPeriodic=0
    g100: GeomPoint X=61.5791 Y=-56.9099 Z=0
    g101: GeomPoint X=58.0728 Y=-62.8351 Z=0
    g102: Circle CenterX=58.0728 CenterY=-77.8102 CenterZ=0 NormalX=0 NormalY=0 NormalZ=1 AngleXU=0 Radius=1
    g103: Circle CenterX=58.0728 CenterY=-81.8102 CenterZ=0 NormalX=0 NormalY=0 NormalZ=1 AngleXU=0 Radius=1
    g104: Circle CenterX=61.1496 CenterY=-79.2541 CenterZ=0 NormalX=0 NormalY=0 NormalZ=1 AngleXU=0 Radius=1
    g105: BSplineCurve PolesCount=3 KnotsCount=2 Degree=2 IsPeriodic=0
    g106: GeomPoint X=58.0728 Y=-77.8102 Z=0
    g107: GeomPoint X=61.1496 Y=-79.2541 Z=0
    g108: LineSegment StartX=58.0728 StartY=-62.8351 StartZ=0 EndX=58.0728 EndY=-77.8102 EndZ=0
    g109: LineSegment StartX=61.1496 StartY=-79.2541 StartZ=0 EndX=127.325 EndY=-24.2775 EndZ=0
    g110: LineSegment StartX=125.607 StartY=-21.7539 StartZ=0 EndX=61.5791 EndY=-56.9099 EndZ=0
    g111: Circle CenterX=302.567 CenterY=-56.9099 CenterZ=0 NormalX=0 NormalY=0 NormalZ=1 AngleXU=0 Radius=1
    g112: Circle CenterX=306.073 CenterY=-58.8351 CenterZ=0 NormalX=0 NormalY=0 NormalZ=1 AngleXU=0 Radius=1
    g113: Circle CenterX=306.073 CenterY=-62.8351 CenterZ=0 NormalX=0 NormalY=0 NormalZ=1 AngleXU=0 Radius=1
    g114: BSplineCurve PolesCount=3 KnotsCount=2 Degree=2 IsPeriodic=0
    g115: GeomPoint X=302.567 Y=-56.9099 Z=0
    g116: GeomPoint X=306.073 Y=-62.8351 Z=0
    g117: Circle CenterX=302.996 CenterY=-79.2541 CenterZ=0 NormalX=0 NormalY=0 NormalZ=1 AngleXU=0 Radius=1
    g118: Circle CenterX=306.073 CenterY=-81.8102 CenterZ=0 NormalX=0 NormalY=0 NormalZ=1 AngleXU=0 Radius=1
    g119: Circle CenterX=306.073 CenterY=-77.8102 CenterZ=0 NormalX=0 NormalY=0 NormalZ=1 AngleXU=0 Radius=1
    g120: BSplineCurve PolesCount=3 KnotsCount=2 Degree=2 IsPeriodic=0
    g121: GeomPoint X=302.996 Y=-79.2541 Z=0
    g122: GeomPoint X=306.073 Y=-77.8102 Z=0
    g123: LineSegment StartX=306.073 StartY=-62.8351 StartZ=0 EndX=306.073 EndY=-77.8102 EndZ=0
    g124: LineSegment StartX=302.996 StartY=-79.2541 StartZ=0 EndX=236.821 EndY=-24.2775 EndZ=0
    g125: LineSegment StartX=238.538 StartY=-21.7539 StartZ=0 EndX=302.567 EndY=-56.9099 EndZ=0
    g126: Circle CenterX=61.6457 CenterY=-88.8112 CenterZ=0 NormalX=0 NormalY=0 NormalZ=1 AngleXU=0 Radius=1
    g127: Circle CenterX=58.0728 CenterY=-91.7794 CenterZ=0 NormalX=0 NormalY=0 NormalZ=1 AngleXU=0 Radius=1
    g128: Circle CenterX=63.9135 CenterY=-91.7794 CenterZ=0 NormalX=0 NormalY=0 NormalZ=1 AngleXU=0 Radius=1
    g129: BSplineCurve PolesCount=3 KnotsCount=2 Degree=2 IsPeriodic=0
    g130: GeomPoint X=61.6457 Y=-88.8112 Z=0
    g131: GeomPoint X=63.9135 Y=-91.7794 Z=0
    g132: Circle CenterX=179.022 CenterY=-85.8163 CenterZ=0 NormalX=0 NormalY=0 NormalZ=1 AngleXU=0 Radius=1
    g133: Circle CenterX=179.022 CenterY=-91.7794 CenterZ=0 NormalX=0 NormalY=0 NormalZ=1 AngleXU=0 Radius=1
    g134: Circle CenterX=171.895 CenterY=-91.7794 CenterZ=0 NormalX=0 NormalY=0 NormalZ=1 AngleXU=0 Radius=1
    g135: BSplineCurve PolesCount=3 KnotsCount=2 Degree=2 IsPeriodic=0
    g136: GeomPoint X=179.022 Y=-85.8163 Z=0
    g137: GeomPoint X=171.895 Y=-91.7794 Z=0
    g138: Circle CenterX=185.124 CenterY=-86.2028 CenterZ=0 NormalX=0 NormalY=0 NormalZ=1 AngleXU=0 Radius=1
    g139: Circle CenterX=185.124 CenterY=-91.7794 CenterZ=0 NormalX=0 NormalY=0 NormalZ=1 AngleXU=0 Radius=1
    g140: Circle CenterX=191.747 CenterY=-91.7794 CenterZ=0 NormalX=0 NormalY=0 NormalZ=1 AngleXU=0 Radius=1
    g141: BSplineCurve PolesCount=3 KnotsCount=2 Degree=2 IsPeriodic=0
    g142: GeomPoint X=185.124 Y=-86.2028 Z=0
    g143: GeomPoint X=191.747 Y=-91.7794 Z=0
    g144: Circle CenterX=299.888 CenterY=-86.6413 CenterZ=0 NormalX=0 NormalY=0 NormalZ=1 AngleXU=0 Radius=1
    g145: Circle CenterX=306.073 CenterY=-91.7794 CenterZ=0 NormalX=0 NormalY=0 NormalZ=1 AngleXU=0 Radius=1
    g146: Circle CenterX=298.776 CenterY=-91.7794 CenterZ=0 NormalX=0 NormalY=0 NormalZ=1 AngleXU=0 Radius=1
    g147: BSplineCurve PolesCount=3 KnotsCount=2 Degree=2 IsPeriodic=0
    g148: GeomPoint X=299.888 Y=-86.6413 Z=0
    g149: GeomPoint X=298.776 Y=-91.7794 Z=0
    g150: LineSegment StartX=189.124 StartY=5.37834 StartZ=0 EndX=299.888 EndY=-86.6413 EndZ=0
    g151: LineSegment StartX=298.776 StartY=-91.7794 StartZ=0 EndX=191.747 EndY=-91.7794 EndZ=0
    g152: LineSegment StartX=185.124 StartY=-86.2028 StartZ=0 EndX=185.124 EndY=5.34704 EndZ=0
    g153: LineSegment StartX=179.022 StartY=5.34704 StartZ=0 EndX=179.022 EndY=-85.8163 EndZ=0
    g154: LineSegment StartX=171.895 StartY=-91.7794 StartZ=0 EndX=63.9135 EndY=-91.7794 EndZ=0
    g155: LineSegment StartX=61.6457 StartY=-88.8112 StartZ=0 EndX=175.022 EndY=5.37834 EndZ=0
    g156: Circle CenterX=302.073 CenterY=124.221 CenterZ=0 NormalX=0 NormalY=0 NormalZ=1 AngleXU=0 Radius=1
    g157: Circle CenterX=306.073 CenterY=124.221 CenterZ=0 NormalX=0 NormalY=0 NormalZ=1 AngleXU=0 Radius=1
    g158: Circle CenterX=302.996 CenterY=121.665 CenterZ=0 NormalX=0 NormalY=0 NormalZ=1 AngleXU=0 Radius=1
    g159: BSplineCurve PolesCount=3 KnotsCount=2 Degree=2 IsPeriodic=0
    g160: GeomPoint X=302.073 Y=124.221 Z=0
    g161: GeomPoint X=302.996 Y=121.665 Z=0
    g162: Circle CenterX=189.124 CenterY=124.221 CenterZ=0 NormalX=0 NormalY=0 NormalZ=1 AngleXU=0 Radius=1
    g163: Circle CenterX=185.124 CenterY=124.221 CenterZ=0 NormalX=0 NormalY=0 NormalZ=1 AngleXU=0 Radius=1
    g164: Circle CenterX=185.124 CenterY=120.221 CenterZ=0 NormalX=0 NormalY=0 NormalZ=1 AngleXU=0 Radius=1
    g165: BSplineCurve PolesCount=3 KnotsCount=2 Degree=2 IsPeriodic=0
    g166: GeomPoint X=189.124 Y=124.221 Z=0
    g167: GeomPoint X=185.124 Y=120.221 Z=0
    g168: Circle CenterX=175.022 CenterY=124.221 CenterZ=0 NormalX=0 NormalY=0 NormalZ=1 AngleXU=0 Radius=1
    g169: Circle CenterX=179.022 CenterY=124.221 CenterZ=0 NormalX=0 NormalY=0 NormalZ=1 AngleXU=0 Radius=1
    g170: Circle CenterX=179.022 CenterY=120.221 CenterZ=0 NormalX=0 NormalY=0 NormalZ=1 AngleXU=0 Radius=1
    g171: BSplineCurve PolesCount=3 KnotsCount=2 Degree=2 IsPeriodic=0
    g172: GeomPoint X=175.022 Y=124.221 Z=0
    g173: GeomPoint X=179.022 Y=120.221 Z=0
    g174: Circle CenterX=62.0728 CenterY=124.221 CenterZ=0 NormalX=0 NormalY=0 NormalZ=1 AngleXU=0 Radius=1
    g175: Circle CenterX=58.0728 CenterY=124.221 CenterZ=0 NormalX=0 NormalY=0 NormalZ=1 AngleXU=0 Radius=1
    g176: Circle CenterX=61.1496 CenterY=121.665 CenterZ=0 NormalX=0 NormalY=0 NormalZ=1 AngleXU=0 Radius=1
    g177: BSplineCurve PolesCount=3 KnotsCount=2 Degree=2 IsPeriodic=0
    g178: GeomPoint X=62.0728 Y=124.221 Z=0
    g179: GeomPoint X=61.1496 Y=121.665 Z=0
    g180: LineSegment StartX=62.0728 StartY=124.221 StartZ=0 EndX=175.022 EndY=124.221 EndZ=0
    g181: LineSegment StartX=179.022 StartY=120.221 StartZ=0 EndX=179.022 EndY=27.0628 EndZ=0
    g182: LineSegment StartX=185.124 StartY=27.0628 StartZ=0 EndX=185.124 EndY=120.221 EndZ=0
    g183: LineSegment StartX=189.124 StartY=124.221 StartZ=0 EndX=302.073 EndY=124.221 EndZ=0
    g184: LineSegment StartX=302.996 StartY=121.665 StartZ=0 EndX=189.124 EndY=27.0628 EndZ=0
    g185: LineSegment StartX=175.022 StartY=27.0628 StartZ=0 EndX=61.1496 EndY=121.665 EndZ=0
    g186: Circle CenterX=61.5791 CenterY=75.4095 CenterZ=0 NormalX=0 NormalY=0 NormalZ=1 AngleXU=0 Radius=1
    g187: Circle CenterX=58.0728 CenterY=77.3346 CenterZ=0 NormalX=0 NormalY=0 NormalZ=1 AngleXU=0 Radius=1
    g188: Circle CenterX=58.0728 CenterY=73.3346 CenterZ=0 NormalX=0 NormalY=0 NormalZ=1 AngleXU=0 Radius=1
    g189: BSplineCurve PolesCount=3 KnotsCount=2 Degree=2 IsPeriodic=0
    g190: GeomPoint X=61.5791 Y=75.4095 Z=0
    g191: GeomPoint X=58.0728 Y=73.3346 Z=0
    g192: Circle CenterX=58.0728 CenterY=-40.8935 CenterZ=0 NormalX=0 NormalY=0 NormalZ=1 AngleXU=0 Radius=1
    g193: Circle CenterX=58.0728 CenterY=-44.8935 CenterZ=0 NormalX=0 NormalY=0 NormalZ=1 AngleXU=0 Radius=1
    g194: Circle CenterX=61.5791 CenterY=-42.9683 CenterZ=0 NormalX=0 NormalY=0 NormalZ=1 AngleXU=0 Radius=1
    g195: BSplineCurve PolesCount=3 KnotsCount=2 Degree=2 IsPeriodic=0
    g196: GeomPoint X=58.0728 Y=-40.8935 Z=0
    g197: GeomPoint X=61.5791 Y=-42.9683 Z=0
    g198: LineSegment StartX=61.5791 StartY=-42.9683 StartZ=0 EndX=165.871 EndY=14.2954 EndZ=0
    g199: LineSegment StartX=165.871 StartY=18.1458 StartZ=0 EndX=61.5791 EndY=75.4095 EndZ=0
    g200: LineSegment StartX=58.0728 StartY=73.3346 StartZ=0 EndX=58.0728 EndY=-40.8935 EndZ=0
    g201: Circle CenterX=302.567 CenterY=-42.9683 CenterZ=0 NormalX=0 NormalY=0 NormalZ=1 AngleXU=0 Radius=1
    g202: Circle CenterX=306.073 CenterY=-44.8935 CenterZ=0 NormalX=0 NormalY=0 NormalZ=1 AngleXU=0 Radius=1
    g203: Circle CenterX=306.073 CenterY=-40.8935 CenterZ=0 NormalX=0 NormalY=0 NormalZ=1 AngleXU=0 Radius=1
    g204: BSplineCurve PolesCount=3 KnotsCount=2 Degree=2 IsPeriodic=0
    g205: GeomPoint X=302.567 Y=-42.9683 Z=0
    g206: GeomPoint X=306.073 Y=-40.8935 Z=0
    g207: Circle CenterX=306.073 CenterY=73.3346 CenterZ=0 NormalX=0 NormalY=0 NormalZ=1 AngleXU=0 Radius=1
    g208: Circle CenterX=306.073 CenterY=77.3346 CenterZ=0 NormalX=0 NormalY=0 NormalZ=1 AngleXU=0 Radius=1
    g209: Circle CenterX=302.567 CenterY=75.4095 CenterZ=0 NormalX=0 NormalY=0 NormalZ=1 AngleXU=0 Radius=1
    g210: BSplineCurve PolesCount=3 KnotsCount=2 Degree=2 IsPeriodic=0
    g211: GeomPoint X=306.073 Y=73.3346 Z=0
    g212: GeomPoint X=302.567 Y=75.4095 Z=0
    g213: LineSegment StartX=302.567 StartY=-42.9683 StartZ=0 EndX=198.275 EndY=14.2954 EndZ=0
    g214: LineSegment StartX=198.275 StartY=18.1458 StartZ=0 EndX=302.567 EndY=75.4095 EndZ=0
    g215: LineSegment StartX=306.073 StartY=73.3346 StartZ=0 EndX=306.073 EndY=-40.8935 EndZ=0
    g216: LineSegment StartX=322.073 StartY=105.865 StartZ=0 EndX=328.643 EndY=105.865 EndZ=0
    g217: LineSegment StartX=318.073 StartY=120.221 StartZ=0 EndX=318.073 EndY=109.865 EndZ=0
    g218: LineSegment StartX=336.157 StartY=107.779 StartZ=0 EndX=362.567 EndY=122.294 EndZ=0
    g219: Circle CenterX=362.073 CenterY=124.221 CenterZ=0 NormalX=0 NormalY=0 NormalZ=1 AngleXU=0 Radius=1
    g220: Circle CenterX=366.073 CenterY=124.221 CenterZ=0 NormalX=0 NormalY=0 NormalZ=1 AngleXU=0 Radius=1
    g221: Circle CenterX=362.567 CenterY=122.294 CenterZ=0 NormalX=0 NormalY=0 NormalZ=1 AngleXU=0 Radius=1
    g222: BSplineCurve PolesCount=3 KnotsCount=2 Degree=2 IsPeriodic=0
    g223: GeomPoint X=362.073 Y=124.221 Z=0
    g224: GeomPoint X=362.567 Y=122.294 Z=0
    g225: Circle CenterX=322.073 CenterY=124.221 CenterZ=0 NormalX=0 NormalY=0 NormalZ=1 AngleXU=0 Radius=1
    g226: Circle CenterX=318.073 CenterY=124.221 CenterZ=0 NormalX=0 NormalY=0 NormalZ=1 AngleXU=0 Radius=1
    g227: Circle CenterX=318.073 CenterY=120.221 CenterZ=0 NormalX=0 NormalY=0 NormalZ=1 AngleXU=0 Radius=1
    g228: BSplineCurve PolesCount=3 KnotsCount=2 Degree=2 IsPeriodic=0
    g229: GeomPoint X=322.073 Y=124.221 Z=0
    g230: GeomPoint X=318.073 Y=120.221 Z=0
    g231: Circle CenterX=322.073 CenterY=105.865 CenterZ=0 NormalX=0 NormalY=0 NormalZ=1 AngleXU=0 Radius=1
    g232: Circle CenterX=318.073 CenterY=105.865 CenterZ=0 NormalX=0 NormalY=0 NormalZ=1 AngleXU=0 Radius=1
    g233: Circle CenterX=318.073 CenterY=109.865 CenterZ=0 NormalX=0 NormalY=0 NormalZ=1 AngleXU=0 Radius=1
    g234: BSplineCurve PolesCount=3 KnotsCount=2 Degree=2 IsPeriodic=0
    g235: GeomPoint X=322.073 Y=105.865 Z=0
    g236: GeomPoint X=318.073 Y=109.865 Z=0
    g237: Circle CenterX=336.157 CenterY=107.779 CenterZ=0 NormalX=0 NormalY=0 NormalZ=1 AngleXU=0 Radius=1
    g238: Circle CenterX=332.651 CenterY=105.853 CenterZ=0 NormalX=0 NormalY=0 NormalZ=1 AngleXU=0 Radius=1
    g239: Circle CenterX=328.643 CenterY=105.865 CenterZ=0 NormalX=0 NormalY=0 NormalZ=1 AngleXU=0 Radius=1
    g240: BSplineCurve PolesCount=3 KnotsCount=2 Degree=2 IsPeriodic=0
    g241: GeomPoint X=336.157 Y=107.779 Z=0
    g242: GeomPoint X=328.643 Y=105.865 Z=0
    g243: LineSegment StartX=322.073 StartY=124.221 StartZ=0 EndX=362.073 EndY=124.221 EndZ=0
    g244: Circle CenterX=371.567 CenterY=-80.8644 CenterZ=0 NormalX=0 NormalY=0 NormalZ=1 AngleXU=0 Radius=1
    g245: Circle CenterX=375.073 CenterY=-82.7896 CenterZ=0 NormalX=0 NormalY=0 NormalZ=1 AngleXU=0 Radius=1
    g246: Circle CenterX=375.073 CenterY=-78.7896 CenterZ=0 NormalX=0 NormalY=0 NormalZ=1 AngleXU=0 Radius=1
    g247: BSplineCurve PolesCount=3 KnotsCount=2 Degree=2 IsPeriodic=0
    g248: GeomPoint X=371.567 Y=-80.8644 Z=0
    g249: GeomPoint X=375.073 Y=-78.7896 Z=0
    g250: Circle CenterX=321.579 CenterY=-53.4075 CenterZ=0 NormalX=0 NormalY=0 NormalZ=1 AngleXU=0 Radius=1
    g251: Circle CenterX=318.073 CenterY=-51.4823 CenterZ=0 NormalX=0 NormalY=0 NormalZ=1 AngleXU=0 Radius=1
    g252: Circle CenterX=318.073 CenterY=-47.4805 CenterZ=0 NormalX=0 NormalY=0 NormalZ=1 AngleXU=0 Radius=1
    g253: BSplineCurve PolesCount=3 KnotsCount=2 Degree=2 IsPeriodic=0
    g254: GeomPoint X=321.579 Y=-53.4075 Z=0
    g255: GeomPoint X=318.073 Y=-47.4805 Z=0
    g256: LineSegment StartX=371.567 StartY=-80.8644 StartZ=0 EndX=321.579 EndY=-53.4075 EndZ=0
    g257: Circle CenterX=321.579 CenterY=-67.3492 CenterZ=0 NormalX=0 NormalY=0 NormalZ=1 AngleXU=0 Radius=1
    g258: Circle CenterX=318.073 CenterY=-65.424 CenterZ=0 NormalX=0 NormalY=0 NormalZ=1 AngleXU=0 Radius=1
    g259: Circle CenterX=318.073 CenterY=-69.424 CenterZ=0 NormalX=0 NormalY=0 NormalZ=1 AngleXU=0 Radius=1
    g260: BSplineCurve PolesCount=3 KnotsCount=2 Degree=2 IsPeriodic=0
    g261: GeomPoint X=321.579 Y=-67.3492 Z=0
    g262: GeomPoint X=318.073 Y=-69.424 Z=0
    g263: Circle CenterX=362.567 CenterY=-89.8542 CenterZ=0 NormalX=0 NormalY=0 NormalZ=1 AngleXU=0 Radius=1
    g264: Circle CenterX=366.073 CenterY=-91.7794 CenterZ=0 NormalX=0 NormalY=0 NormalZ=1 AngleXU=0 Radius=1
    g265: Circle CenterX=362.073 CenterY=-91.7794 CenterZ=0 NormalX=0 NormalY=0 NormalZ=1 AngleXU=0 Radius=1
    g266: BSplineCurve PolesCount=3 KnotsCount=2 Degree=2 IsPeriodic=0
    g267: GeomPoint X=362.567 Y=-89.8542 Z=0
    g268: GeomPoint X=362.073 Y=-91.7794 Z=0
    g269: Circle CenterX=322.073 CenterY=-91.7794 CenterZ=0 NormalX=0 NormalY=0 NormalZ=1 AngleXU=0 Radius=1
    g270: Circle CenterX=318.073 CenterY=-91.7794 CenterZ=0 NormalX=0 NormalY=0 NormalZ=1 AngleXU=0 Radius=1
    g271: Circle CenterX=318.073 CenterY=-87.7794 CenterZ=0 NormalX=0 NormalY=0 NormalZ=1 AngleXU=0 Radius=1
    g272: BSplineCurve PolesCount=3 KnotsCount=2 Degree=2 IsPeriodic=0
    g273: GeomPoint X=322.073 Y=-91.7794 Z=0
    g274: GeomPoint X=318.073 Y=-87.7794 Z=0
    g275: LineSegment StartX=362.567 StartY=-89.8542 StartZ=0 EndX=321.579 EndY=-67.3492 EndZ=0
    g276: LineSegment StartX=318.073 StartY=-69.424 StartZ=0 EndX=318.073 EndY=-87.7794 EndZ=0
    g277: LineSegment StartX=322.073 StartY=-91.7794 StartZ=0 EndX=362.073 EndY=-91.7794 EndZ=0
    g278: Circle CenterX=2.07281 CenterY=124.221 CenterZ=0 NormalX=0 NormalY=0 NormalZ=1 AngleXU=0 Radius=1
    g279: Circle CenterX=1.57905 CenterY=122.295 CenterZ=0 NormalX=0 NormalY=0 NormalZ=1 AngleXU=0 Radius=1
    g280: BSplineCurve PolesCount=3 KnotsCount=2 Degree=2 IsPeriodic=0
    g281: GeomPoint X=2.07281 Y=124.221 Z=0
    g282: GeomPoint X=1.57905 Y=122.295 Z=0
    g283: Circle CenterX=42.0728 CenterY=124.221 CenterZ=0 NormalX=0 NormalY=0 NormalZ=1 AngleXU=0 Radius=1
    g284: Circle CenterX=46.0728 CenterY=124.221 CenterZ=0 NormalX=0 NormalY=0 NormalZ=1 AngleXU=0 Radius=1
    g285: Circle CenterX=46.0728 CenterY=120.221 CenterZ=0 NormalX=0 NormalY=0 NormalZ=1 AngleXU=0 Radius=1
    g286: BSplineCurve PolesCount=3 KnotsCount=2 Degree=2 IsPeriodic=0
    g287: GeomPoint X=42.0728 Y=124.221 Z=0
    g288: GeomPoint X=46.0728 Y=120.221 Z=0
    g289: Circle CenterX=46.0728 CenterY=109.865 CenterZ=0 NormalX=0 NormalY=0 NormalZ=1 AngleXU=0 Radius=1
    g290: Circle CenterX=46.0728 CenterY=105.865 CenterZ=0 NormalX=0 NormalY=0 NormalZ=1 AngleXU=0 Radius=1
    g291: Circle CenterX=42.0728 CenterY=105.865 CenterZ=0 NormalX=0 NormalY=0 NormalZ=1 AngleXU=0 Radius=1
    g292: BSplineCurve PolesCount=3 KnotsCount=2 Degree=2 IsPeriodic=0
    g293: GeomPoint X=46.0728 Y=109.865 Z=0
    g294: GeomPoint X=42.0728 Y=105.865 Z=0
    g295: Circle CenterX=35.5028 CenterY=105.865 CenterZ=0 NormalX=0 NormalY=0 NormalZ=1 AngleXU=0 Radius=1
    g296: Circle CenterX=31.5028 CenterY=105.865 CenterZ=0 NormalX=0 NormalY=0 NormalZ=1 AngleXU=0 Radius=1
    g297: Circle CenterX=27.9965 CenterY=107.79 CenterZ=0 NormalX=0 NormalY=0 NormalZ=1 AngleXU=0 Radius=1
    g298: BSplineCurve PolesCount=3 KnotsCount=2 Degree=2 IsPeriodic=0
    g299: GeomPoint X=35.5028 Y=105.865 Z=0
    g300: GeomPoint X=27.9965 Y=107.79 Z=0
    g301: LineSegment StartX=2.07281 StartY=124.221 StartZ=0 EndX=42.0728 EndY=124.221 EndZ=0
    g302: LineSegment StartX=46.0728 StartY=120.221 StartZ=0 EndX=46.0728 EndY=109.865 EndZ=0
    g303: LineSegment StartX=42.0728 StartY=105.865 StartZ=0 EndX=35.5028 EndY=105.865 EndZ=0
    g304: LineSegment StartX=27.9965 StartY=107.79 StartZ=0 EndX=1.57905 EndY=122.295 EndZ=0
    g305: Circle CenterX=42.5666 CenterY=-67.3492 CenterZ=0 NormalX=0 NormalY=0 NormalZ=1 AngleXU=0 Radius=1
    g306: Circle CenterX=46.0728 CenterY=-65.424 CenterZ=0 NormalX=0 NormalY=0 NormalZ=1 AngleXU=0 Radius=1
    g307: Circle CenterX=46.0728 CenterY=-69.424 CenterZ=0 NormalX=0 NormalY=0 NormalZ=1 AngleXU=0 Radius=1
    g308: BSplineCurve PolesCount=3 KnotsCount=2 Degree=2 IsPeriodic=0
    g309: GeomPoint X=42.5666 Y=-67.3492 Z=0
    g310: GeomPoint X=46.0728 Y=-69.424 Z=0
    g311: Circle CenterX=46.0728 CenterY=-87.7794 CenterZ=0 NormalX=0 NormalY=0 NormalZ=1 AngleXU=0 Radius=1
    g312: Circle CenterX=46.0728 CenterY=-91.7794 CenterZ=0 NormalX=0 NormalY=0 NormalZ=1 AngleXU=0 Radius=1
    g313: Circle CenterX=42.0728 CenterY=-91.7794 CenterZ=0 NormalX=0 NormalY=0 NormalZ=1 AngleXU=0 Radius=1
    g314: BSplineCurve PolesCount=3 KnotsCount=2 Degree=2 IsPeriodic=0
    g315: GeomPoint X=46.0728 Y=-87.7794 Z=0
    g316: GeomPoint X=42.0728 Y=-91.7794 Z=0
    g317: Circle CenterX=2.07281 CenterY=-91.7794 CenterZ=0 NormalX=0 NormalY=0 NormalZ=1 AngleXU=0 Radius=1
    g318: Circle CenterX=-1.92719 CenterY=-91.7794 CenterZ=0 NormalX=0 NormalY=0 NormalZ=1 AngleXU=0 Radius=1
    g319: Circle CenterX=1.57905 CenterY=-89.8542 CenterZ=0 NormalX=0 NormalY=0 NormalZ=1 AngleXU=0 Radius=1
    g320: BSplineCurve PolesCount=3 KnotsCount=2 Degree=2 IsPeriodic=0
    g321: GeomPoint X=2.07281 Y=-91.7794 Z=0
    g322: GeomPoint X=1.57905 Y=-89.8542 Z=0
    g323: LineSegment StartX=2.07281 StartY=-91.7794 StartZ=0 EndX=42.0728 EndY=-91.7794 EndZ=0
    g324: LineSegment StartX=46.0728 StartY=-87.7794 StartZ=0 EndX=46.0728 EndY=-69.424 EndZ=0
    g325: LineSegment StartX=42.5666 StartY=-67.3492 StartZ=0 EndX=1.57905 EndY=-89.8542 EndZ=0
    g326: Circle CenterX=322.073 CenterY=76.4095 CenterZ=0 NormalX=0 NormalY=0 NormalZ=1 AngleXU=0 Radius=4
    g327: BSplineCurve PolesCount=3 KnotsCount=2 Degree=2 IsPeriodic=0
    g328: GeomPoint X=318.073 Y=72.4095 Z=0
    g329: GeomPoint X=322.073 Y=76.4095 Z=0
    g330: Circle CenterX=375.073 CenterY=72.4095 CenterZ=0 NormalX=0 NormalY=0 NormalZ=1 AngleXU=0 Radius=1
    g331: Circle CenterX=375.073 CenterY=76.4095 CenterZ=0 NormalX=0 NormalY=0 NormalZ=1 AngleXU=0 Radius=1
    g332: Circle CenterX=371.073 CenterY=76.4095 CenterZ=0 NormalX=0 NormalY=0 NormalZ=1 AngleXU=0 Radius=1
    g333: BSplineCurve PolesCount=3 KnotsCount=2 Degree=2 IsPeriodic=0
    g334: GeomPoint X=375.073 Y=72.4095 Z=0
    g335: GeomPoint X=371.073 Y=76.4095 Z=0
    g336: LineSegment StartX=322.073 StartY=76.4095 StartZ=0 EndX=371.073 EndY=76.4095 EndZ=0
    g337: LineSegment StartX=318.073 StartY=72.4095 StartZ=0 EndX=318.073 EndY=-47.4805 EndZ=0
    g338: LineSegment StartX=375.073 StartY=72.4095 StartZ=0 EndX=375.073 EndY=-78.7896 EndZ=0
    g339: ArcOfCircle CenterX=-26.9272 CenterY=22.1087 CenterZ=0 NormalX=0 NormalY=0 NormalZ=1 AngleXU=0 Radius=4 StartAngle=5e-16 EndAngle=3.14159
    g340: LineSegment StartX=-22.9272 StartY=22.1087 StartZ=0 EndX=-18.9272 EndY=-83.7794 EndZ=0
    g341: LineSegment StartX=-34.9272 StartY=-83.7794 StartZ=0 EndX=-30.9272 EndY=22.1087 EndZ=0
    g342: ArcOfCircle CenterX=391.073 CenterY=22.1087 CenterZ=0 NormalX=0 NormalY=0 NormalZ=1 AngleXU=0 Radius=4 StartAngle=0 EndAngle=3.14159
    g343: LineSegment StartX=387.073 StartY=22.1087 StartZ=0 EndX=383.073 EndY=-83.7794 EndZ=0
    g344: LineSegment StartX=395.073 StartY=22.1087 StartZ=0 EndX=399.073 EndY=-83.7794 EndZ=0
    g345: Circle CenterX=-10.9272 CenterY=-78.7794 CenterZ=0 NormalX=0 NormalY=0 NormalZ=1 AngleXU=0 Radius=1
    g346: Circle CenterX=-10.9272 CenterY=-82.7794 CenterZ=0 NormalX=0 NormalY=0 NormalZ=1 AngleXU=0 Radius=1
    g347: Circle CenterX=-7.42095 CenterY=-80.8542 CenterZ=0 NormalX=0 NormalY=0 NormalZ=1 AngleXU=0 Radius=1
    g348: BSplineCurve PolesCount=3 KnotsCount=2 Degree=2 IsPeriodic=0
    g349: GeomPoint X=-10.9272 Y=-78.7794 Z=0
    g350: GeomPoint X=-7.42095 Y=-80.8542 Z=0
    g351: Circle CenterX=42.5666 CenterY=-53.4075 CenterZ=0 NormalX=0 NormalY=0 NormalZ=1 AngleXU=0 Radius=1
    g352: Circle CenterX=46.0728 CenterY=-51.4823 CenterZ=0 NormalX=0 NormalY=0 NormalZ=1 AngleXU=0 Radius=1
    g353: Circle CenterX=46.0728 CenterY=-47.4823 CenterZ=0 NormalX=0 NormalY=0 NormalZ=1 AngleXU=0 Radius=1
    g354: BSplineCurve PolesCount=3 KnotsCount=2 Degree=2 IsPeriodic=0
    g355: GeomPoint X=42.5666 Y=-53.4075 Z=0
    g356: GeomPoint X=46.0728 Y=-47.4823 Z=0
    g357: Circle CenterX=46.0728 CenterY=72.4095 CenterZ=0 NormalX=0 NormalY=0 NormalZ=1 AngleXU=0 Radius=1
    g358: Circle CenterX=46.0728 CenterY=76.4095 CenterZ=0 NormalX=0 NormalY=0 NormalZ=1 AngleXU=0 Radius=1
    g359: Circle CenterX=42.0728 CenterY=76.4095 CenterZ=0 NormalX=0 NormalY=0 NormalZ=1 AngleXU=0 Radius=1
    g360: BSplineCurve PolesCount=3 KnotsCount=2 Degree=2 IsPeriodic=0
    g361: GeomPoint X=46.0728 Y=72.4095 Z=0
    g362: GeomPoint X=42.0728 Y=76.4095 Z=0
    g363: Circle CenterX=-6.92718 CenterY=76.4095 CenterZ=0 NormalX=0 NormalY=0 NormalZ=1 AngleXU=0 Radius=1
    g364: Circle CenterX=-10.9272 CenterY=76.4095 CenterZ=0 NormalX=0 NormalY=0 NormalZ=1 AngleXU=0 Radius=1
    g365: Circle CenterX=-10.9272 CenterY=72.4095 CenterZ=0 NormalX=0 NormalY=0 NormalZ=1 AngleXU=0 Radius=1
    g366: BSplineCurve PolesCount=3 KnotsCount=2 Degree=2 IsPeriodic=0
    g367: GeomPoint X=-6.92718 Y=76.4095 Z=0
    g368: GeomPoint X=-10.9272 Y=72.4095 Z=0
    g369: LineSegment StartX=-10.9272 StartY=72.4095 StartZ=0 EndX=-10.9272 EndY=-78.7794 EndZ=0
    g370: LineSegment StartX=-7.42095 StartY=-80.8542 StartZ=0 EndX=42.5666 EndY=-53.4075 EndZ=0
    g371: LineSegment StartX=46.0728 StartY=-47.4823 StartZ=0 EndX=46.0728 EndY=72.4095 EndZ=0
    g372: LineSegment StartX=42.0728 StartY=76.4095 StartZ=0 EndX=-6.92719 EndY=76.4095 EndZ=0
  constraints (613):
    c: Vertical(g0)
    c: Vertical(g1)
    c: Block(g1)
    c: Block(g0)
    c: Weight(g4) = 1
    c: Equal(g4,g5)
    c: Equal(g4,g6)
    c: InternalAlignment(g4,g7)
    c: InternalAlignment(g5,g7)
    c: InternalAlignment(g6,g7)
    c: InternalAlignment(g8,g7)
    c: InternalAlignment(g9,g7)
    c: Weight(g10) = 1
    c: Equal(g10,g11)
    c: Equal(g10,g12)
    c: InternalAlignment(g10,g13)
    c: InternalAlignment(g11,g13)
    c: InternalAlignment(g12,g13)
    c: InternalAlignment(g14,g13)
    c: InternalAlignment(g15,g13)
    c: Block(g13)
    c: Block(g7)
    c: Weight(g16) = 1
    c: Equal(g16,g17)
    c: Equal(g16,g18)
    c: InternalAlignment(g16,g19)
    c: InternalAlignment(g17,g19)
    c: InternalAlignment(g18,g19)
    c: InternalAlignment(g20,g19)
    c: InternalAlignment(g21,g19)
    c: Weight(g22) = 1
    c: Equal(g22,g23)
    c: Equal(g22,g24)
    c: InternalAlignment(g22,g25)
    c: InternalAlignment(g23,g25)
    c: InternalAlignment(g24,g25)
    c: InternalAlignment(g26,g25)
    c: InternalAlignment(g27,g25)
    c: Block(g25)
    c: Block(g19)
    c: Weight(g28) = 1
    c: Equal(g28,g29)
    c: Equal(g28,g30)
    c: InternalAlignment(g28,g31)
    c: InternalAlignment(g29,g31)
    c: InternalAlignment(g30,g31)
    c: InternalAlignment(g32,g31)
    c: InternalAlignment(g33,g31)
    c: Weight(g34) = 1
    c: Equal(g34,g35)
    c: Equal(g34,g36)
    c: InternalAlignment(g34,g37)
    c: InternalAlignment(g35,g37)
    c: InternalAlignment(g36,g37)
    c: InternalAlignment(g38,g37)
    c: InternalAlignment(g39,g37)
    c: Block(g31)
    c: Block(g37)
    c: Coincident(g40,g1)
    c: Coincident(g40,g0)
    c: Horizontal(g40)
    c: Distance(g40) = 450
    c: Coincident(g41,g1)
    c: Coincident(g41,g0)
    c: Horizontal(g41)
    c: Weight(g42) = 1
    c: Equal(g42,g43)
    c: Equal(g42,g44)
    c: InternalAlignment(g42,g45)
    c: InternalAlignment(g43,g45)
    c: InternalAlignment(g44,g45)
    c: InternalAlignment(g46,g45)
    c: InternalAlignment(g47,g45)
    c: Block(g45)
    c: Weight(g48) = 1
    c: Equal(g48,g49)
    c: Equal(g48,g50)
    c: InternalAlignment(g48,g51)
    c: InternalAlignment(g49,g51)
    c: InternalAlignment(g50,g51)
    c: InternalAlignment(g52,g51)
    c: InternalAlignment(g53,g51)
    c: Block(g51)
    c: Weight(g54) = 1
    c: Equal(g54,g55)
    c: Equal(g54,g56)
    c: InternalAlignment(g54,g57)
    c: InternalAlignment(g55,g57)
    c: InternalAlignment(g56,g57)
    c: InternalAlignment(g58,g57)
    c: InternalAlignment(g59,g57)
    c: Block(g57)
    c: Weight(g60) = 1
    c: Equal(g60,g61)
    c: Equal(g60,g62)
    c: InternalAlignment(g60,g63)
    c: InternalAlignment(g61,g63)
    c: InternalAlignment(g62,g63)
    c: InternalAlignment(g64,g63)
    c: InternalAlignment(g65,g63)
    c: Block(g63)
    c: Weight(g66) = 1
    c: Equal(g66,g67)
    c: Equal(g66,g68)
    c: InternalAlignment(g66,g69)
    c: InternalAlignment(g67,g69)
    c: InternalAlignment(g68,g69)
    c: InternalAlignment(g70,g69)
    c: InternalAlignment(g71,g69)
    c: Weight(g72) = 1
    c: Equal(g72,g73)
    c: Equal(g72,g74)
    c: InternalAlignment(g72,g75)
    c: InternalAlignment(g73,g75)
    c: InternalAlignment(g74,g75)
    c: InternalAlignment(g76,g75)
    c: InternalAlignment(g77,g75)
    c: Block(g69)
    c: Block(g75)
    c: Coincident(g78,g69)
    c: Coincident(g78,g75)
    c: Vertical(g78)
    c: Coincident(g79,g69)
    c: Coincident(g79,g51)
    c: Coincident(g80,g51)
    c: Coincident(g80,g75)
    c: Weight(g81) = 1
    c: Equal(g81,g82)
    c: Equal(g81,g83)
    c: InternalAlignment(g81,g84)
    c: InternalAlignment(g82,g84)
    c: InternalAlignment(g83,g84)
    c: InternalAlignment(g85,g84)
    c: InternalAlignment(g86,g84)
    c: Weight(g87) = 1
    c: Equal(g87,g88)
    c: Equal(g87,g89)
    c: InternalAlignment(g87,g90)
    c: InternalAlignment(g88,g90)
    c: InternalAlignment(g89,g90)
    c: InternalAlignment(g91,g90)
    c: InternalAlignment(g92,g90)
    c: Block(g84)
    c: Block(g90)
    c: Coincident(g93,g84)
    c: Coincident(g93,g90)
    c: Vertical(g93)
    c: Coincident(g94,g84)
    c: Coincident(g94,g45)
    c: Coincident(g95,g45)
    c: Coincident(g95,g90)
    c: Weight(g96) = 1
    c: Equal(g96,g97)
    c: Equal(g96,g98)
    c: InternalAlignment(g96,g99)
    c: InternalAlignment(g97,g99)
    c: InternalAlignment(g98,g99)
    c: InternalAlignment(g100,g99)
    c: InternalAlignment(g101,g99)
    c: Weight(g102) = 1
    c: Equal(g102,g103)
    c: Equal(g102,g104)
    c: InternalAlignment(g102,g105)
    c: InternalAlignment(g103,g105)
    c: InternalAlignment(g104,g105)
    c: InternalAlignment(g106,g105)
    c: InternalAlignment(g107,g105)
    c: Block(g99)
    c: Block(g105)
    c: Coincident(g108,g99)
    c: Coincident(g108,g105)
    c: Vertical(g108)
    c: Coincident(g109,g105)
    c: Coincident(g109,g63)
    c: Coincident(g110,g63)
    c: Coincident(g110,g99)
    c: Weight(g111) = 1
    c: Equal(g111,g112)
    c: Equal(g111,g113)
    c: InternalAlignment(g111,g114)
    c: InternalAlignment(g112,g114)
    c: InternalAlignment(g113,g114)
    c: InternalAlignment(g115,g114)
    c: InternalAlignment(g116,g114)
    c: Weight(g117) = 1
    c: Equal(g117,g118)
    c: Equal(g117,g119)
    c: InternalAlignment(g117,g120)
    c: InternalAlignment(g118,g120)
    c: InternalAlignment(g119,g120)
    c: InternalAlignment(g121,g120)
    c: InternalAlignment(g122,g120)
    c: Block(g114)
    c: Block(g120)
    c: Coincident(g123,g114)
    c: Coincident(g123,g120)
    c: Vertical(g123)
    c: Coincident(g124,g120)
    c: Coincident(g124,g57)
    c: Coincident(g125,g57)
    c: Coincident(g125,g114)
    c: Weight(g126) = 1
    c: Equal(g126,g127)
    c: Equal(g126,g128)
    c: InternalAlignment(g126,g129)
    c: InternalAlignment(g127,g129)
    c: InternalAlignment(g128,g129)
    c: InternalAlignment(g130,g129)
    c: InternalAlignment(g131,g129)
    c: Weight(g132) = 1
    c: Equal(g132,g133)
    c: Equal(g132,g134)
    c: InternalAlignment(g132,g135)
    c: InternalAlignment(g133,g135)
    c: InternalAlignment(g134,g135)
    c: InternalAlignment(g136,g135)
    c: InternalAlignment(g137,g135)
    c: Weight(g138) = 1
    c: Equal(g138,g139)
    c: Equal(g138,g140)
    c: InternalAlignment(g138,g141)
    c: InternalAlignment(g139,g141)
    c: InternalAlignment(g140,g141)
    c: InternalAlignment(g142,g141)
    c: InternalAlignment(g143,g141)
    c: Weight(g144) = 1
    c: Equal(g144,g145)
    c: Equal(g144,g146)
    c: InternalAlignment(g144,g147)
    c: InternalAlignment(g145,g147)
    c: InternalAlignment(g146,g147)
    c: InternalAlignment(g148,g147)
    c: InternalAlignment(g149,g147)
    c: Block(g147)
    c: Block(g141)
    c: Block(g135)
    c: Block(g129)
    c: Coincident(g150,g25)
    c: Coincident(g150,g147)
    c: Coincident(g151,g147)
    c: Coincident(g151,g141)
    c: Horizontal(g151)
    c: Coincident(g152,g141)
    c: Coincident(g152,g25)
    c: Vertical(g152)
    c: Coincident(g153,g19)
    c: Coincident(g153,g135)
    c: Vertical(g153)
    c: Coincident(g154,g135)
    c: Coincident(g154,g129)
    c: Horizontal(g154)
    c: Coincident(g155,g129)
    c: Coincident(g155,g19)
    c: Weight(g156) = 1
    c: Equal(g156,g157)
    c: Equal(g156,g158)
    c: InternalAlignment(g156,g159)
    c: InternalAlignment(g157,g159)
    c: InternalAlignment(g158,g159)
    c: InternalAlignment(g160,g159)
    c: InternalAlignment(g161,g159)
    c: Weight(g162) = 1
    c: Equal(g162,g163)
    c: Equal(g162,g164)
    c: InternalAlignment(g162,g165)
    c: InternalAlignment(g163,g165)
    c: InternalAlignment(g164,g165)
    c: InternalAlignment(g166,g165)
    c: InternalAlignment(g167,g165)
    c: Weight(g168) = 1
    c: Equal(g168,g169)
    c: Equal(g168,g170)
    c: InternalAlignment(g168,g171)
    c: InternalAlignment(g169,g171)
    c: InternalAlignment(g170,g171)
    c: InternalAlignment(g172,g171)
    c: InternalAlignment(g173,g171)
    c: Weight(g174) = 1
    c: Equal(g174,g175)
    c: Equal(g174,g176)
    c: InternalAlignment(g174,g177)
    c: InternalAlignment(g175,g177)
    c: InternalAlignment(g176,g177)
    c: InternalAlignment(g178,g177)
    c: InternalAlignment(g179,g177)
    c: Block(g177)
    c: Block(g171)
    c: Block(g165)
    c: Block(g159)
    c: Coincident(g180,g177)
    c: Coincident(g180,g171)
    c: Horizontal(g180)
    c: Coincident(g181,g171)
    c: Coincident(g181,g7)
    c: Vertical(g181)
    c: Coincident(g182,g13)
    c: Coincident(g182,g165)
    c: Vertical(g182)
    c: Coincident(g183,g165)
    c: Coincident(g183,g159)
    c: Horizontal(g183)
    c: Coincident(g184,g159)
    c: Coincident(g184,g13)
    c: Coincident(g185,g7)
    c: Weight(g186) = 1
    c: Equal(g186,g187)
    c: Equal(g186,g188)
    c: InternalAlignment(g186,g189)
    c: InternalAlignment(g187,g189)
    c: InternalAlignment(g188,g189)
    c: InternalAlignment(g190,g189)
    c: InternalAlignment(g191,g189)
    c: Weight(g192) = 1
    c: Equal(g192,g193)
    c: Equal(g192,g194)
    c: InternalAlignment(g192,g195)
    c: InternalAlignment(g193,g195)
    c: InternalAlignment(g194,g195)
    c: InternalAlignment(g196,g195)
    c: InternalAlignment(g197,g195)
    c: Block(g195)
    c: Block(g189)
    c: Coincident(g198,g195)
    c: Coincident(g198,g31)
    c: Coincident(g199,g31)
    c: Coincident(g199,g189)
    c: Coincident(g200,g189)
    c: Coincident(g200,g195)
    c: Vertical(g200)
    c: Weight(g201) = 1
    c: Equal(g201,g202)
    c: Equal(g201,g203)
    c: InternalAlignment(g201,g204)
    c: InternalAlignment(g202,g204)
    c: InternalAlignment(g203,g204)
    c: InternalAlignment(g205,g204)
    c: InternalAlignment(g206,g204)
    c: Weight(g207) = 1
    c: Equal(g207,g208)
    c: Equal(g207,g209)
    c: InternalAlignment(g207,g210)
    c: InternalAlignment(g208,g210)
    c: InternalAlignment(g209,g210)
    c: InternalAlignment(g211,g210)
    c: InternalAlignment(g212,g210)
    c: Block(g210)
    c: Block(g204)
    c: Coincident(g213,g204)
    c: Coincident(g213,g37)
    c: Coincident(g214,g37)
    c: Coincident(g214,g210)
    c: Coincident(g215,g210)
    c: Coincident(g215,g204)
    c: Vertical(g215)
    c: Horizontal(g216)
    c: Block(g216)
    c: Vertical(g217)
    c: Block(g217)
    c: Block(g218)
    c: Weight(g219) = 1
    c: Equal(g219,g220)
    c: Equal(g219,g221)
    c: InternalAlignment(g219,g222)
    c: InternalAlignment(g220,g222)
    c: InternalAlignment(g221,g222)
    c: InternalAlignment(g223,g222)
    c: InternalAlignment(g224,g222)
    c: Weight(g225) = 1
    c: Equal(g225,g226)
    c: Equal(g225,g227)
    c: InternalAlignment(g225,g228)
    c: InternalAlignment(g226,g228)
    c: InternalAlignment(g227,g228)
    c: InternalAlignment(g229,g228)
    c: InternalAlignment(g230,g228)
    c: Weight(g231) = 1
    c: Equal(g231,g232)
    c: Equal(g231,g233)
    c: InternalAlignment(g231,g234)
    c: InternalAlignment(g232,g234)
    c: InternalAlignment(g233,g234)
    c: InternalAlignment(g235,g234)
    c: InternalAlignment(g236,g234)
    c: Weight(g237) = 1
    c: Equal(g237,g238)
    c: Equal(g237,g239)
    c: InternalAlignment(g237,g240)
    c: InternalAlignment(g238,g240)
    c: InternalAlignment(g239,g240)
    c: InternalAlignment(g241,g240)
    c: InternalAlignment(g242,g240)
    c: Block(g222)
    c: Block(g228)
    c: Block(g234)
    c: Block(g240)
    c: Coincident(g243,g228)
    c: Coincident(g243,g222)
    c: Horizontal(g243)
    c: Block(g185)
    c: Weight(g244) = 1
    c: Equal(g244,g245)
    c: Equal(g244,g246)
    c: InternalAlignment(g244,g247)
    c: InternalAlignment(g245,g247)
    c: InternalAlignment(g246,g247)
    c: InternalAlignment(g248,g247)
    c: InternalAlignment(g249,g247)
    c: Weight(g250) = 1
    c: Equal(g250,g251)
    c: Equal(g250,g252)
    c: InternalAlignment(g250,g253)
    c: InternalAlignment(g251,g253)
    c: InternalAlignment(g252,g253)
    c: InternalAlignment(g254,g253)
    c: InternalAlignment(g255,g253)
    c: Block(g247)
    c: Block(g253)
    c: Coincident(g256,g247)
    c: Coincident(g256,g253)
    c: Weight(g257) = 1
    c: Equal(g257,g258)
    c: Equal(g257,g259)
    c: InternalAlignment(g257,g260)
    c: InternalAlignment(g258,g260)
    c: InternalAlignment(g259,g260)
    c: InternalAlignment(g261,g260)
    c: InternalAlignment(g262,g260)
    c: Weight(g263) = 1
    c: Equal(g263,g264)
    c: Equal(g263,g265)
    c: InternalAlignment(g263,g266)
    c: InternalAlignment(g264,g266)
    c: InternalAlignment(g265,g266)
    c: InternalAlignment(g267,g266)
    c: InternalAlignment(g268,g266)
    c: Weight(g269) = 1
    c: Equal(g269,g270)
    c: Equal(g269,g271)
    c: InternalAlignment(g269,g272)
    c: InternalAlignment(g270,g272)
    c: InternalAlignment(g271,g272)
    c: InternalAlignment(g273,g272)
    c: InternalAlignment(g274,g272)
    c: Block(g272)
    c: Block(g266)
    c: Block(g260)
    c: Coincident(g275,g266)
    c: Coincident(g275,g260)
    c: Coincident(g276,g260)
    c: Coincident(g276,g272)
    c: Vertical(g276)
    c: Coincident(g277,g272)
    c: Coincident(g277,g266)
    c: Horizontal(g277)
    c: Weight(g278) = 1
    c: Equal(g278,g279)
    c: InternalAlignment(g278,g280)
    c: InternalAlignment(g279,g280)
    c: InternalAlignment(g281,g280)
    c: InternalAlignment(g282,g280)
    c: Weight(g283) = 1
    c: InternalAlignment(g284,g286)
    c: InternalAlignment(g285,g286)
    c: InternalAlignment(g287,g286)
    c: InternalAlignment(g288,g286)
    c: Weight(g289) = 1
    c: Equal(g289,g290)
    c: Equal(g289,g291)
    c: InternalAlignment(g289,g292)
    c: InternalAlignment(g290,g292)
    c: InternalAlignment(g291,g292)
    c: InternalAlignment(g293,g292)
    c: InternalAlignment(g294,g292)
    c: Equal(g295,g296)
    c: Equal(g295,g297)
    c: InternalAlignment(g295,g298)
    c: InternalAlignment(g296,g298)
    c: InternalAlignment(g297,g298)
    c: InternalAlignment(g299,g298)
    c: InternalAlignment(g300,g298)
    c: Block(g286)
    c: Block(g292)
    c: Block(g298)
    c: Block(g280)
    c: Coincident(g301,g280)
    c: Coincident(g301,g286)
    c: Horizontal(g301)
    c: Coincident(g302,g286)
    c: Coincident(g302,g292)
    c: Vertical(g302)
    c: Coincident(g303,g292)
    c: Coincident(g303,g298)
    c: Horizontal(g303)
    c: Coincident(g304,g298)
    c: Coincident(g304,g280)
    c: Weight(g305) = 1
    c: Equal(g305,g306)
    c: Equal(g305,g307)
    c: InternalAlignment(g305,g308)
    c: InternalAlignment(g306,g308)
    c: InternalAlignment(g307,g308)
    c: InternalAlignment(g309,g308)
    c: InternalAlignment(g310,g308)
    c: Weight(g311) = 1
    c: Equal(g311,g312)
    c: Equal(g311,g313)
    c: InternalAlignment(g311,g314)
    c: InternalAlignment(g312,g314)
    c: InternalAlignment(g313,g314)
    c: InternalAlignment(g315,g314)
    c: InternalAlignment(g316,g314)
    c: Weight(g317) = 1
    c: Equal(g317,g318)
    c: Equal(g317,g319)
    c: InternalAlignment(g317,g320)
    c: InternalAlignment(g318,g320)
    c: InternalAlignment(g319,g320)
    c: InternalAlignment(g321,g320)
    c: InternalAlignment(g322,g320)
    c: Block(g320)
    c: Block(g314)
    c: Block(g308)
    c: Coincident(g323,g320)
    c: Coincident(g323,g314)
    c: Horizontal(g323)
    c: Coincident(g324,g314)
    c: Coincident(g324,g308)
    c: Vertical(g324)
    c: Coincident(g325,g308)
    c: Coincident(g325,g320)
    c: InternalAlignment(g326,g327)
    c: InternalAlignment(g328,g327)
    c: InternalAlignment(g329,g327)
    c: Block(g327)
    c: Equal(g330,g331)
    c: Equal(g330,g332)
    c: InternalAlignment(g330,g333)
    c: InternalAlignment(g331,g333)
    c: InternalAlignment(g332,g333)
    c: InternalAlignment(g334,g333)
    c: InternalAlignment(g335,g333)
    c: Block(g333)
    c: Coincident(g336,g327)
    c: Horizontal(g336)
    c: Block(g336)
    c: Coincident(g337,g327)
    c: Coincident(g337,g253)
    c: Vertical(g337)
    c: Coincident(g338,g333)
    c: Coincident(g338,g247)
    c: Vertical(g338)
    c: Block(g339)
    c: Block(g2)
    c: Distance(g337) = 119.89
    c: Coincident(g340,g339)
    c: Coincident(g340,g2)
    c: Coincident(g341,g2)
    c: Coincident(g341,g339)
    c: Block(g3)
    c: Block(g342)
    c: Coincident(g343,g342)
    c: Coincident(g343,g3)
    c: Coincident(g344,g342)
    c: Coincident(g344,g3)
    c: Block(g344)
    c: Block(g343)
    c: Weight(g345) = 1
    c: Equal(g345,g346)
    c: Equal(g345,g347)
    c: InternalAlignment(g345,g348)
    c: InternalAlignment(g346,g348)
    c: InternalAlignment(g347,g348)
    c: InternalAlignment(g349,g348)
    c: InternalAlignment(g350,g348)
    c: Weight(g351) = 1
    c: Equal(g351,g352)
    c: Equal(g351,g353)
    c: InternalAlignment(g351,g354)
    c: InternalAlignment(g352,g354)
    c: InternalAlignment(g353,g354)
    c: InternalAlignment(g355,g354)
    c: InternalAlignment(g356,g354)
    c: Weight(g357) = 1
    c: Equal(g357,g358)
    c: Equal(g357,g359)
    c: InternalAlignment(g357,g360)
    c: InternalAlignment(g358,g360)
    c: InternalAlignment(g359,g360)
    c: InternalAlignment(g361,g360)
    c: InternalAlignment(g362,g360)
    c: Weight(g363) = 1
    c: Equal(g363,g364)
    c: Equal(g363,g365)
    c: InternalAlignment(g363,g366)
    c: InternalAlignment(g364,g366)
    c: InternalAlignment(g365,g366)
    c: InternalAlignment(g367,g366)
    c: InternalAlignment(g368,g366)
    c: Block(g366)
    c: Block(g360)
    c: Block(g354)
    c: Block(g348)
    c: Coincident(g369,g366)
    c: Coincident(g369,g348)
    c: Vertical(g369)
    c: Coincident(g370,g348)
    c: Coincident(g370,g354)
    c: Coincident(g371,g354)
    c: Coincident(g371,g360)
    c: Vertical(g371)
    c: Coincident(g372,g360)
    c: Coincident(g372,g366)
    c: Horizontal(g372)
